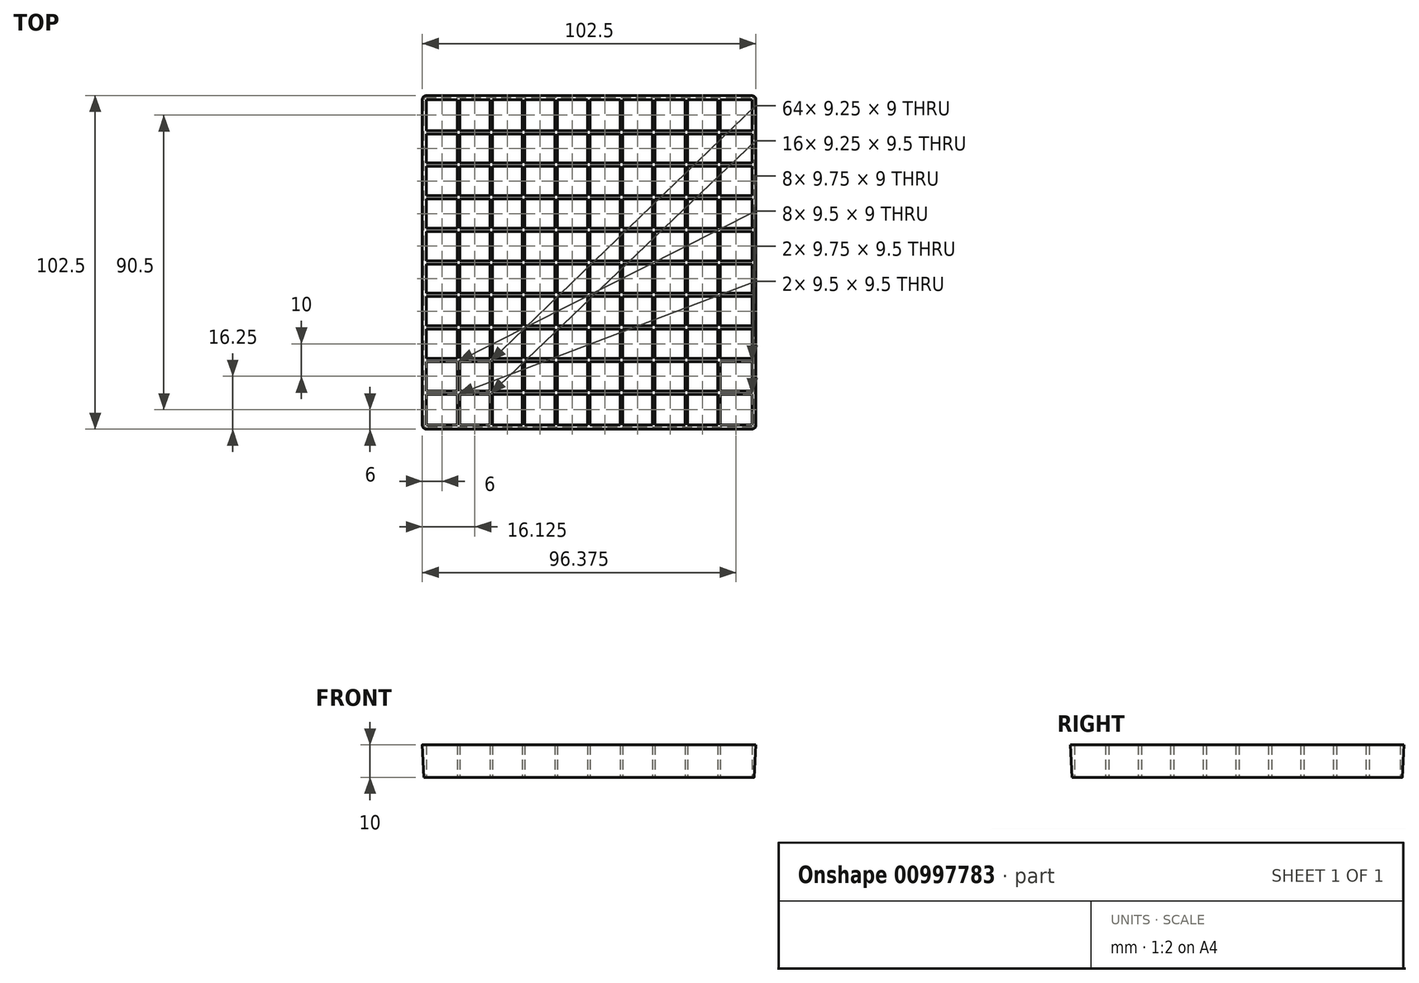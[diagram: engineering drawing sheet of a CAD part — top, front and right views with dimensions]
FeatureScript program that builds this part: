
annotation { "Feature Type Name" : "Feature", "Feature Type Description" : "" }
export const myFeature = defineFeature(function(context is Context, id is Id, definition is map)
    precondition{}
    {
        {
            assignVariable(context, id + "F0", {"name" : "p", "anyValue" : 1.5});
        }
        {
            var Q0;
            Q0=qCreatedBy(makeId("Top.planeOp"),FACE);
            var sketch = newSketch(context, id + "F1", { "sketchPlane" : qUnion([Q0])});
            skLineSegment(sketch, "E0.bottom", {"start": v(50, 50) * mm, "end": v(-50, 50) * mm});
            skLineSegment(sketch, "E0.top", {"start": v(50, -50) * mm, "end": v(-50, -50) * mm});
            skLineSegment(sketch, "E0.left", {"start": v(50, 50) * mm, "end": v(50, -50) * mm});
            skLineSegment(sketch, "E0.right", {"start": v(-50, 50) * mm, "end": v(-50, -50) * mm});
            skPoint(sketch, "E0.middle", {"position": v(0, 0) * mm});
            skLineSegment(sketch, "E1.bottom", {"start": v(-51.5, 51.5) * mm, "end": v(51.5, 51.5) * mm});
            skLineSegment(sketch, "E1.top", {"start": v(-51.5, -51.5) * mm, "end": v(51.5, -51.5) * mm});
            skLineSegment(sketch, "E1.left", {"start": v(-51.5, 51.5) * mm, "end": v(-51.5, -51.5) * mm});
            skLineSegment(sketch, "E1.right", {"start": v(51.5, 51.5) * mm, "end": v(51.5, -51.5) * mm});
            skLineSegment(sketch, "E2.bottom", {"start": v(-40.5, 50) * mm, "end": v(-39.75, 50) * mm});
            skLineSegment(sketch, "E2.top", {"start": v(-40.5, -50) * mm, "end": v(-39.75, -50) * mm});
            skLineSegment(sketch, "E2.left", {"start": v(-40.5, 50) * mm, "end": v(-40.5, -50) * mm});
            skLineSegment(sketch, "E2.right", {"start": v(-39.75, 50) * mm, "end": v(-39.75, -50) * mm});
            skLineSegment(sketch, "E3.1.0.0", {"start": v(-30.5, 50) * mm, "end": v(-30.5, -50) * mm});
            skLineSegment(sketch, "E3.1.0.1", {"start": v(-29.75, 50) * mm, "end": v(-29.75, -50) * mm});
            skLineSegment(sketch, "E3.2.0.0", {"start": v(-20.5, 50) * mm, "end": v(-20.5, -50) * mm});
            skLineSegment(sketch, "E3.2.0.1", {"start": v(-19.75, 50) * mm, "end": v(-19.75, -50) * mm});
            skLineSegment(sketch, "E3.3.0.0", {"start": v(-10.5, 50) * mm, "end": v(-10.5, -50) * mm});
            skLineSegment(sketch, "E3.3.0.1", {"start": v(-9.75, 50) * mm, "end": v(-9.75, -50) * mm});
            skLineSegment(sketch, "E3.4.0.0", {"start": v(-0.5, 50) * mm, "end": v(-0.5, -50) * mm});
            skLineSegment(sketch, "E3.4.0.1", {"start": v(0.25, 50) * mm, "end": v(0.25, -50) * mm});
            skLineSegment(sketch, "E3.5.0.0", {"start": v(9.5, 50) * mm, "end": v(9.5, -50) * mm});
            skLineSegment(sketch, "E3.5.0.1", {"start": v(10.25, 50) * mm, "end": v(10.25, -50) * mm});
            skLineSegment(sketch, "E3.6.0.0", {"start": v(19.5, 50) * mm, "end": v(19.5, -50) * mm});
            skLineSegment(sketch, "E3.6.0.1", {"start": v(20.25, 50) * mm, "end": v(20.25, -50) * mm});
            skLineSegment(sketch, "E3.7.0.0", {"start": v(29.5, 50) * mm, "end": v(29.5, -50) * mm});
            skLineSegment(sketch, "E3.7.0.1", {"start": v(30.25, 50) * mm, "end": v(30.25, -50) * mm});
            skLineSegment(sketch, "E3.8.0.0", {"start": v(39.5, 50) * mm, "end": v(39.5, -50) * mm});
            skLineSegment(sketch, "E3.8.0.1", {"start": v(40.25, 50) * mm, "end": v(40.25, -50) * mm});
            skLineSegment(sketch, "E3.direction1", {"start": v(-40.5, -50) * mm, "end": v(-30.5, -50) * mm, "construction": true});
            skLineSegment(sketch, "E4.bottom", {"start": v(-50, 40.5) * mm, "end": v(50, 40.5) * mm});
            skLineSegment(sketch, "E4.top", {"start": v(-50, 39.5) * mm, "end": v(50, 39.5) * mm});
            skLineSegment(sketch, "E4.left", {"start": v(-50, 40.5) * mm, "end": v(-50, 39.5) * mm});
            skLineSegment(sketch, "E4.right", {"start": v(50, 40.5) * mm, "end": v(50, 39.5) * mm});
            skLineSegment(sketch, "E5.0.1.0", {"start": v(-50, 30.5) * mm, "end": v(50, 30.5) * mm});
            skLineSegment(sketch, "E5.0.1.1", {"start": v(-50, 29.5) * mm, "end": v(50, 29.5) * mm});
            skLineSegment(sketch, "E5.0.2.0", {"start": v(-50, 20.5) * mm, "end": v(50, 20.5) * mm});
            skLineSegment(sketch, "E5.0.2.1", {"start": v(-50, 19.5) * mm, "end": v(50, 19.5) * mm});
            skLineSegment(sketch, "E5.0.3.0", {"start": v(-50, 10.5) * mm, "end": v(50, 10.5) * mm});
            skLineSegment(sketch, "E5.0.3.1", {"start": v(-50, 9.5) * mm, "end": v(50, 9.5) * mm});
            skLineSegment(sketch, "E5.0.4.0", {"start": v(-50, 0.5) * mm, "end": v(50, 0.5) * mm});
            skLineSegment(sketch, "E5.0.4.1", {"start": v(-50, -0.5) * mm, "end": v(50, -0.5) * mm});
            skLineSegment(sketch, "E5.0.5.0", {"start": v(-50, -9.5) * mm, "end": v(50, -9.5) * mm});
            skLineSegment(sketch, "E5.0.5.1", {"start": v(-50, -10.5) * mm, "end": v(50, -10.5) * mm});
            skLineSegment(sketch, "E5.0.6.0", {"start": v(-50, -19.5) * mm, "end": v(50, -19.5) * mm});
            skLineSegment(sketch, "E5.0.6.1", {"start": v(-50, -20.5) * mm, "end": v(50, -20.5) * mm});
            skLineSegment(sketch, "E5.0.7.0", {"start": v(-50, -29.5) * mm, "end": v(50, -29.5) * mm});
            skLineSegment(sketch, "E5.0.7.1", {"start": v(-50, -30.5) * mm, "end": v(50, -30.5) * mm});
            skLineSegment(sketch, "E5.0.8.0", {"start": v(-50, -39.5) * mm, "end": v(50, -39.5) * mm});
            skLineSegment(sketch, "E5.0.8.1", {"start": v(-50, -40.5) * mm, "end": v(50, -40.5) * mm});
            skLineSegment(sketch, "E5.direction1", {"start": v(-50, 40.5) * mm, "end": v(-25, 40.5) * mm, "construction": true});
            skLineSegment(sketch, "E5.direction2", {"start": v(-50, 40.5) * mm, "end": v(-50, 30.5) * mm, "construction": true});
            skSolve(sketch);
        }
        {
            var Q0;
            Q0=makeQuery(id+"F1.imprint","IMPRINT",FACE,{"disambiguationData":[TD([[makeQuery(id+"F1.imprint","IMPRINT",EDGE,{"derivedFrom":sQuery(id+"F1.wireOp",EDGE,"E1.bottom")}),-1.0]])]});
            extrude(context, id + "F2", {"entities" : qUnion([Q0]), "depth" : 10 * mm, "offsetDistance" : 25 * mm});
        }
        {
            var Q0;
            {var subQ0=sQuery(id+"F1.wireOp",EDGE,"E5.0.5.1");var subQ1=sQuery(id+"F1.wireOp",EDGE,"E3.1.0.0");var subQ2=makeQuery(id+"F1.imprint","INTERSECT",VERTEX,{"derivedFrom":[subQ1,subQ0]});Q0=makeQuery(id+"F1.imprint","IMPRINT",FACE,{"disambiguationData":[TD([[makeQuery(id+"F1.imprint","IMPRINT",EDGE,{"disambiguationData":[TD([[subQ2,-1.0]])],"derivedFrom":subQ1}),1.0]])]});}
            var Q1;
            {var subQ0=sQuery(id+"F1.wireOp",EDGE,"E5.0.6.1");var subQ1=sQuery(id+"F1.wireOp",EDGE,"E3.1.0.0");var subQ2=makeQuery(id+"F1.imprint","INTERSECT",VERTEX,{"derivedFrom":[subQ1,subQ0]});Q1=makeQuery(id+"F1.imprint","IMPRINT",FACE,{"disambiguationData":[TD([[makeQuery(id+"F1.imprint","IMPRINT",EDGE,{"disambiguationData":[TD([[subQ2,1.0]])],"derivedFrom":subQ1}),1.0]])]});}
            var Q2;
            {var subQ0=sQuery(id+"F1.wireOp",EDGE,"E5.0.2.1");var subQ1=sQuery(id+"F1.wireOp",EDGE,"E3.7.0.0");var subQ2=makeQuery(id+"F1.imprint","INTERSECT",VERTEX,{"derivedFrom":[subQ1,subQ0]});Q2=makeQuery(id+"F1.imprint","IMPRINT",FACE,{"disambiguationData":[TD([[makeQuery(id+"F1.imprint","IMPRINT",EDGE,{"disambiguationData":[TD([[subQ2,1.0]])],"derivedFrom":subQ1}),1.0]])]});}
            var Q3;
            {var subQ0=sQuery(id+"F1.wireOp",EDGE,"E5.0.4.0");var subQ1=sQuery(id+"F1.wireOp",EDGE,"E2.right");var subQ2=makeQuery(id+"F1.imprint","INTERSECT",VERTEX,{"derivedFrom":[subQ1,subQ0]});Q3=makeQuery(id+"F1.imprint","IMPRINT",FACE,{"disambiguationData":[TD([[makeQuery(id+"F1.imprint","IMPRINT",EDGE,{"disambiguationData":[TD([[subQ2,-1.0]])],"derivedFrom":subQ1}),1.0]])]});}
            var Q4;
            {var subQ0=sQuery(id+"F1.wireOp",EDGE,"E5.0.7.0");var subQ1=sQuery(id+"F1.wireOp",EDGE,"E3.1.0.1");var subQ2=makeQuery(id+"F1.imprint","INTERSECT",VERTEX,{"derivedFrom":[subQ1,subQ0]});Q4=makeQuery(id+"F1.imprint","IMPRINT",FACE,{"disambiguationData":[TD([[makeQuery(id+"F1.imprint","IMPRINT",EDGE,{"disambiguationData":[TD([[subQ2,-1.0]])],"derivedFrom":subQ1}),1.0]])]});}
            var Q5;
            {var subQ0=sQuery(id+"F1.wireOp",EDGE,"E5.0.5.0");var subQ1=sQuery(id+"F1.wireOp",EDGE,"E3.4.0.0");var subQ2=makeQuery(id+"F1.imprint","INTERSECT",VERTEX,{"derivedFrom":[subQ1,subQ0]});Q5=makeQuery(id+"F1.imprint","IMPRINT",FACE,{"disambiguationData":[TD([[makeQuery(id+"F1.imprint","IMPRINT",EDGE,{"disambiguationData":[TD([[subQ2,1.0]])],"derivedFrom":subQ1}),1.0]])]});}
            var Q6;
            {var subQ0=sQuery(id+"F1.wireOp",EDGE,"E5.0.7.0");var subQ1=sQuery(id+"F1.wireOp",EDGE,"E3.1.0.0");var subQ2=makeQuery(id+"F1.imprint","INTERSECT",VERTEX,{"derivedFrom":[subQ1,subQ0]});Q6=makeQuery(id+"F1.imprint","IMPRINT",FACE,{"disambiguationData":[TD([[makeQuery(id+"F1.imprint","IMPRINT",EDGE,{"disambiguationData":[TD([[subQ2,1.0]])],"derivedFrom":subQ1}),1.0]])]});}
            var Q7;
            {var subQ0=sQuery(id+"F1.wireOp",EDGE,"E5.0.5.0");var subQ1=sQuery(id+"F1.wireOp",EDGE,"E3.1.0.1");var subQ2=makeQuery(id+"F1.imprint","INTERSECT",VERTEX,{"derivedFrom":[subQ1,subQ0]});Q7=makeQuery(id+"F1.imprint","IMPRINT",FACE,{"disambiguationData":[TD([[makeQuery(id+"F1.imprint","IMPRINT",EDGE,{"disambiguationData":[TD([[subQ2,-1.0]])],"derivedFrom":subQ1}),1.0]])]});}
            var Q8;
            {var subQ0=sQuery(id+"F1.wireOp",EDGE,"E5.0.1.1");var subQ1=sQuery(id+"F1.wireOp",EDGE,"E2.left");var subQ2=makeQuery(id+"F1.imprint","INTERSECT",VERTEX,{"derivedFrom":[subQ1,subQ0]});Q8=makeQuery(id+"F1.imprint","IMPRINT",FACE,{"disambiguationData":[TD([[makeQuery(id+"F1.imprint","IMPRINT",EDGE,{"disambiguationData":[TD([[subQ2,1.0]])],"derivedFrom":subQ1}),1.0]])]});}
            var Q9;
            {var subQ0=sQuery(id+"F1.wireOp",EDGE,"E5.0.2.1");var subQ1=sQuery(id+"F1.wireOp",EDGE,"E3.4.0.1");var subQ2=makeQuery(id+"F1.imprint","INTERSECT",VERTEX,{"derivedFrom":[subQ1,subQ0]});Q9=makeQuery(id+"F1.imprint","IMPRINT",FACE,{"disambiguationData":[TD([[makeQuery(id+"F1.imprint","IMPRINT",EDGE,{"disambiguationData":[TD([[subQ2,1.0]])],"derivedFrom":subQ1}),1.0]])]});}
            var Q10;
            {var subQ0=sQuery(id+"F1.wireOp",EDGE,"E5.0.1.0");var subQ1=sQuery(id+"F1.wireOp",EDGE,"E3.1.0.1");var subQ2=makeQuery(id+"F1.imprint","INTERSECT",VERTEX,{"derivedFrom":[subQ1,subQ0]});Q10=makeQuery(id+"F1.imprint","IMPRINT",FACE,{"disambiguationData":[TD([[makeQuery(id+"F1.imprint","IMPRINT",EDGE,{"disambiguationData":[TD([[subQ2,-1.0]])],"derivedFrom":subQ1}),1.0]])]});}
            var Q11;
            {var subQ0=sQuery(id+"F1.wireOp",EDGE,"E5.0.8.0");var subQ1=sQuery(id+"F1.wireOp",EDGE,"E3.6.0.0");var subQ2=makeQuery(id+"F1.imprint","INTERSECT",VERTEX,{"derivedFrom":[subQ1,subQ0]});Q11=makeQuery(id+"F1.imprint","IMPRINT",FACE,{"disambiguationData":[TD([[makeQuery(id+"F1.imprint","IMPRINT",EDGE,{"disambiguationData":[TD([[subQ2,1.0]])],"derivedFrom":subQ1}),1.0]])]});}
            var Q12;
            {var subQ0=sQuery(id+"F1.wireOp",EDGE,"E5.0.1.1");var subQ1=sQuery(id+"F1.wireOp",EDGE,"E2.right");var subQ2=makeQuery(id+"F1.imprint","INTERSECT",VERTEX,{"derivedFrom":[subQ1,subQ0]});Q12=makeQuery(id+"F1.imprint","IMPRINT",FACE,{"disambiguationData":[TD([[makeQuery(id+"F1.imprint","IMPRINT",EDGE,{"disambiguationData":[TD([[subQ2,1.0]])],"derivedFrom":subQ1}),1.0]])]});}
            var Q13;
            {var subQ0=sQuery(id+"F1.wireOp",EDGE,"E5.0.3.1");var subQ1=sQuery(id+"F1.wireOp",EDGE,"E3.8.0.0");var subQ2=makeQuery(id+"F1.imprint","INTERSECT",VERTEX,{"derivedFrom":[subQ1,subQ0]});Q13=makeQuery(id+"F1.imprint","IMPRINT",FACE,{"disambiguationData":[TD([[makeQuery(id+"F1.imprint","IMPRINT",EDGE,{"disambiguationData":[TD([[subQ2,1.0]])],"derivedFrom":subQ1}),1.0]])]});}
            var Q14;
            {var subQ0=sQuery(id+"F1.wireOp",EDGE,"E5.0.2.0");var subQ1=sQuery(id+"F1.wireOp",EDGE,"E3.1.0.0");var subQ2=makeQuery(id+"F1.imprint","INTERSECT",VERTEX,{"derivedFrom":[subQ1,subQ0]});Q14=makeQuery(id+"F1.imprint","IMPRINT",FACE,{"disambiguationData":[TD([[makeQuery(id+"F1.imprint","IMPRINT",EDGE,{"disambiguationData":[TD([[subQ2,-1.0]])],"derivedFrom":subQ1}),1.0]])]});}
            var Q15;
            {var subQ0=sQuery(id+"F1.wireOp",EDGE,"E5.0.6.1");var subQ1=sQuery(id+"F1.wireOp",EDGE,"E3.2.0.0");var subQ2=makeQuery(id+"F1.imprint","INTERSECT",VERTEX,{"derivedFrom":[subQ1,subQ0]});Q15=makeQuery(id+"F1.imprint","IMPRINT",FACE,{"disambiguationData":[TD([[makeQuery(id+"F1.imprint","IMPRINT",EDGE,{"disambiguationData":[TD([[subQ2,1.0]])],"derivedFrom":subQ1}),1.0]])]});}
            var Q16;
            {var subQ0=sQuery(id+"F1.wireOp",EDGE,"E5.0.4.0");var subQ1=sQuery(id+"F1.wireOp",EDGE,"E3.1.0.1");var subQ2=makeQuery(id+"F1.imprint","INTERSECT",VERTEX,{"derivedFrom":[subQ1,subQ0]});Q16=makeQuery(id+"F1.imprint","IMPRINT",FACE,{"disambiguationData":[TD([[makeQuery(id+"F1.imprint","IMPRINT",EDGE,{"disambiguationData":[TD([[subQ2,-1.0]])],"derivedFrom":subQ1}),1.0]])]});}
            var Q17;
            {var subQ0=sQuery(id+"F1.wireOp",EDGE,"E5.0.6.0");var subQ1=sQuery(id+"F1.wireOp",EDGE,"E3.8.0.0");var subQ2=makeQuery(id+"F1.imprint","INTERSECT",VERTEX,{"derivedFrom":[subQ1,subQ0]});Q17=makeQuery(id+"F1.imprint","IMPRINT",FACE,{"disambiguationData":[TD([[makeQuery(id+"F1.imprint","IMPRINT",EDGE,{"disambiguationData":[TD([[subQ2,1.0]])],"derivedFrom":subQ1}),1.0]])]});}
            var Q18;
            {var subQ0=sQuery(id+"F1.wireOp",EDGE,"E5.0.4.1");var subQ1=sQuery(id+"F1.wireOp",EDGE,"E3.6.0.1");var subQ2=makeQuery(id+"F1.imprint","INTERSECT",VERTEX,{"derivedFrom":[subQ1,subQ0]});Q18=makeQuery(id+"F1.imprint","IMPRINT",FACE,{"disambiguationData":[TD([[makeQuery(id+"F1.imprint","IMPRINT",EDGE,{"disambiguationData":[TD([[subQ2,1.0]])],"derivedFrom":subQ1}),1.0]])]});}
            var Q19;
            {var subQ0=sQuery(id+"F1.wireOp",EDGE,"E5.0.3.1");var subQ1=sQuery(id+"F1.wireOp",EDGE,"E3.4.0.0");var subQ2=makeQuery(id+"F1.imprint","INTERSECT",VERTEX,{"derivedFrom":[subQ1,subQ0]});Q19=makeQuery(id+"F1.imprint","IMPRINT",FACE,{"disambiguationData":[TD([[makeQuery(id+"F1.imprint","IMPRINT",EDGE,{"disambiguationData":[TD([[subQ2,1.0]])],"derivedFrom":subQ1}),1.0]])]});}
            var Q20;
            {var subQ0=sQuery(id+"F1.wireOp",EDGE,"E5.0.7.0");var subQ1=sQuery(id+"F1.wireOp",EDGE,"E3.3.0.1");var subQ2=makeQuery(id+"F1.imprint","INTERSECT",VERTEX,{"derivedFrom":[subQ1,subQ0]});Q20=makeQuery(id+"F1.imprint","IMPRINT",FACE,{"disambiguationData":[TD([[makeQuery(id+"F1.imprint","IMPRINT",EDGE,{"disambiguationData":[TD([[subQ2,-1.0]])],"derivedFrom":subQ1}),1.0]])]});}
            var Q21;
            {var subQ0=sQuery(id+"F1.wireOp",EDGE,"E5.0.1.1");var subQ1=sQuery(id+"F1.wireOp",EDGE,"E3.5.0.0");var subQ2=makeQuery(id+"F1.imprint","INTERSECT",VERTEX,{"derivedFrom":[subQ1,subQ0]});Q21=makeQuery(id+"F1.imprint","IMPRINT",FACE,{"disambiguationData":[TD([[makeQuery(id+"F1.imprint","IMPRINT",EDGE,{"disambiguationData":[TD([[subQ2,1.0]])],"derivedFrom":subQ1}),1.0]])]});}
            var Q22;
            {var subQ0=sQuery(id+"F1.wireOp",EDGE,"E5.0.1.1");var subQ1=sQuery(id+"F1.wireOp",EDGE,"E3.6.0.1");var subQ2=makeQuery(id+"F1.imprint","INTERSECT",VERTEX,{"derivedFrom":[subQ1,subQ0]});Q22=makeQuery(id+"F1.imprint","IMPRINT",FACE,{"disambiguationData":[TD([[makeQuery(id+"F1.imprint","IMPRINT",EDGE,{"disambiguationData":[TD([[subQ2,1.0]])],"derivedFrom":subQ1}),1.0]])]});}
            var Q23;
            {var subQ0=sQuery(id+"F1.wireOp",EDGE,"E4.bottom");var subQ1=sQuery(id+"F1.wireOp",EDGE,"E3.8.0.0");var subQ2=makeQuery(id+"F1.imprint","INTERSECT",VERTEX,{"derivedFrom":[subQ1,subQ0]});Q23=makeQuery(id+"F1.imprint","IMPRINT",FACE,{"disambiguationData":[TD([[makeQuery(id+"F1.imprint","IMPRINT",EDGE,{"disambiguationData":[TD([[subQ2,-1.0]])],"derivedFrom":subQ1}),1.0]])]});}
            var Q24;
            {var subQ0=sQuery(id+"F1.wireOp",EDGE,"E5.0.2.0");var subQ1=sQuery(id+"F1.wireOp",EDGE,"E3.7.0.1");var subQ2=makeQuery(id+"F1.imprint","INTERSECT",VERTEX,{"derivedFrom":[subQ1,subQ0]});Q24=makeQuery(id+"F1.imprint","IMPRINT",FACE,{"disambiguationData":[TD([[makeQuery(id+"F1.imprint","IMPRINT",EDGE,{"disambiguationData":[TD([[subQ2,-1.0]])],"derivedFrom":subQ1}),1.0]])]});}
            var Q25;
            {var subQ0=sQuery(id+"F1.wireOp",EDGE,"E5.0.5.1");var subQ1=sQuery(id+"F1.wireOp",EDGE,"E3.5.0.0");var subQ2=makeQuery(id+"F1.imprint","INTERSECT",VERTEX,{"derivedFrom":[subQ1,subQ0]});Q25=makeQuery(id+"F1.imprint","IMPRINT",FACE,{"disambiguationData":[TD([[makeQuery(id+"F1.imprint","IMPRINT",EDGE,{"disambiguationData":[TD([[subQ2,-1.0]])],"derivedFrom":subQ1}),1.0]])]});}
            var Q26;
            {var subQ0=sQuery(id+"F1.wireOp",EDGE,"E5.0.5.1");var subQ1=sQuery(id+"F1.wireOp",EDGE,"E3.6.0.0");var subQ2=makeQuery(id+"F1.imprint","INTERSECT",VERTEX,{"derivedFrom":[subQ1,subQ0]});Q26=makeQuery(id+"F1.imprint","IMPRINT",FACE,{"disambiguationData":[TD([[makeQuery(id+"F1.imprint","IMPRINT",EDGE,{"disambiguationData":[TD([[subQ2,-1.0]])],"derivedFrom":subQ1}),1.0]])]});}
            var Q27;
            {var subQ0=sQuery(id+"F1.wireOp",EDGE,"E5.0.2.0");var subQ1=sQuery(id+"F1.wireOp",EDGE,"E2.left");var subQ2=makeQuery(id+"F1.imprint","INTERSECT",VERTEX,{"derivedFrom":[subQ1,subQ0]});Q27=makeQuery(id+"F1.imprint","IMPRINT",FACE,{"disambiguationData":[TD([[makeQuery(id+"F1.imprint","IMPRINT",EDGE,{"disambiguationData":[TD([[subQ2,1.0]])],"derivedFrom":subQ1}),1.0]])]});}
            var Q28;
            {var subQ0=sQuery(id+"F1.wireOp",EDGE,"E5.0.4.1");var subQ1=sQuery(id+"F1.wireOp",EDGE,"E3.6.0.0");var subQ2=makeQuery(id+"F1.imprint","INTERSECT",VERTEX,{"derivedFrom":[subQ1,subQ0]});Q28=makeQuery(id+"F1.imprint","IMPRINT",FACE,{"disambiguationData":[TD([[makeQuery(id+"F1.imprint","IMPRINT",EDGE,{"disambiguationData":[TD([[subQ2,1.0]])],"derivedFrom":subQ1}),1.0]])]});}
            var Q29;
            {var subQ0=sQuery(id+"F1.wireOp",EDGE,"E5.0.6.1");var subQ1=sQuery(id+"F1.wireOp",EDGE,"E3.5.0.0");var subQ2=makeQuery(id+"F1.imprint","INTERSECT",VERTEX,{"derivedFrom":[subQ1,subQ0]});Q29=makeQuery(id+"F1.imprint","IMPRINT",FACE,{"disambiguationData":[TD([[makeQuery(id+"F1.imprint","IMPRINT",EDGE,{"disambiguationData":[TD([[subQ2,1.0]])],"derivedFrom":subQ1}),1.0]])]});}
            var Q30;
            {var subQ0=sQuery(id+"F1.wireOp",EDGE,"E4.top");var subQ1=sQuery(id+"F1.wireOp",EDGE,"E3.4.0.1");var subQ2=makeQuery(id+"F1.imprint","INTERSECT",VERTEX,{"derivedFrom":[subQ1,subQ0]});Q30=makeQuery(id+"F1.imprint","IMPRINT",FACE,{"disambiguationData":[TD([[makeQuery(id+"F1.imprint","IMPRINT",EDGE,{"disambiguationData":[TD([[subQ2,1.0]])],"derivedFrom":subQ1}),1.0]])]});}
            var Q31;
            {var subQ0=sQuery(id+"F1.wireOp",EDGE,"E5.0.1.1");var subQ1=sQuery(id+"F1.wireOp",EDGE,"E3.2.0.0");var subQ2=makeQuery(id+"F1.imprint","INTERSECT",VERTEX,{"derivedFrom":[subQ1,subQ0]});Q31=makeQuery(id+"F1.imprint","IMPRINT",FACE,{"disambiguationData":[TD([[makeQuery(id+"F1.imprint","IMPRINT",EDGE,{"disambiguationData":[TD([[subQ2,-1.0]])],"derivedFrom":subQ1}),1.0]])]});}
            var Q32;
            {var subQ0=sQuery(id+"F1.wireOp",EDGE,"E5.0.1.1");var subQ1=sQuery(id+"F1.wireOp",EDGE,"E3.4.0.0");var subQ2=makeQuery(id+"F1.imprint","INTERSECT",VERTEX,{"derivedFrom":[subQ1,subQ0]});Q32=makeQuery(id+"F1.imprint","IMPRINT",FACE,{"disambiguationData":[TD([[makeQuery(id+"F1.imprint","IMPRINT",EDGE,{"disambiguationData":[TD([[subQ2,1.0]])],"derivedFrom":subQ1}),1.0]])]});}
            var Q33;
            {var subQ0=sQuery(id+"F1.wireOp",EDGE,"E4.top");var subQ1=sQuery(id+"F1.wireOp",EDGE,"E3.4.0.0");var subQ2=makeQuery(id+"F1.imprint","INTERSECT",VERTEX,{"derivedFrom":[subQ1,subQ0]});Q33=makeQuery(id+"F1.imprint","IMPRINT",FACE,{"disambiguationData":[TD([[makeQuery(id+"F1.imprint","IMPRINT",EDGE,{"disambiguationData":[TD([[subQ2,-1.0]])],"derivedFrom":subQ1}),1.0]])]});}
            var Q34;
            {var subQ0=sQuery(id+"F1.wireOp",EDGE,"E5.0.7.0");var subQ1=sQuery(id+"F1.wireOp",EDGE,"E3.5.0.0");var subQ2=makeQuery(id+"F1.imprint","INTERSECT",VERTEX,{"derivedFrom":[subQ1,subQ0]});Q34=makeQuery(id+"F1.imprint","IMPRINT",FACE,{"disambiguationData":[TD([[makeQuery(id+"F1.imprint","IMPRINT",EDGE,{"disambiguationData":[TD([[subQ2,-1.0]])],"derivedFrom":subQ1}),1.0]])]});}
            var Q35;
            {var subQ0=sQuery(id+"F1.wireOp",EDGE,"E5.0.1.1");var subQ1=sQuery(id+"F1.wireOp",EDGE,"E3.5.0.1");var subQ2=makeQuery(id+"F1.imprint","INTERSECT",VERTEX,{"derivedFrom":[subQ1,subQ0]});Q35=makeQuery(id+"F1.imprint","IMPRINT",FACE,{"disambiguationData":[TD([[makeQuery(id+"F1.imprint","IMPRINT",EDGE,{"disambiguationData":[TD([[subQ2,1.0]])],"derivedFrom":subQ1}),1.0]])]});}
            var Q36;
            {var subQ0=sQuery(id+"F1.wireOp",EDGE,"E5.0.5.0");var subQ1=sQuery(id+"F1.wireOp",EDGE,"E3.5.0.0");var subQ2=makeQuery(id+"F1.imprint","INTERSECT",VERTEX,{"derivedFrom":[subQ1,subQ0]});Q36=makeQuery(id+"F1.imprint","IMPRINT",FACE,{"disambiguationData":[TD([[makeQuery(id+"F1.imprint","IMPRINT",EDGE,{"disambiguationData":[TD([[subQ2,1.0]])],"derivedFrom":subQ1}),1.0]])]});}
            var Q37;
            {var subQ0=sQuery(id+"F1.wireOp",EDGE,"E5.0.8.1");var subQ1=sQuery(id+"F1.wireOp",EDGE,"E3.2.0.1");var subQ2=makeQuery(id+"F1.imprint","INTERSECT",VERTEX,{"derivedFrom":[subQ1,subQ0]});Q37=makeQuery(id+"F1.imprint","IMPRINT",FACE,{"disambiguationData":[TD([[makeQuery(id+"F1.imprint","IMPRINT",EDGE,{"disambiguationData":[TD([[subQ2,1.0]])],"derivedFrom":subQ1}),1.0]])]});}
            var Q38;
            {var subQ0=sQuery(id+"F1.wireOp",EDGE,"E5.0.6.1");var subQ1=sQuery(id+"F1.wireOp",EDGE,"E3.6.0.1");var subQ2=makeQuery(id+"F1.imprint","INTERSECT",VERTEX,{"derivedFrom":[subQ1,subQ0]});Q38=makeQuery(id+"F1.imprint","IMPRINT",FACE,{"disambiguationData":[TD([[makeQuery(id+"F1.imprint","IMPRINT",EDGE,{"disambiguationData":[TD([[subQ2,1.0]])],"derivedFrom":subQ1}),1.0]])]});}
            var Q39;
            {var subQ0=sQuery(id+"F1.wireOp",EDGE,"E4.bottom");var subQ1=sQuery(id+"F1.wireOp",EDGE,"E2.right");var subQ2=makeQuery(id+"F1.imprint","INTERSECT",VERTEX,{"derivedFrom":[subQ1,subQ0]});Q39=makeQuery(id+"F1.imprint","IMPRINT",FACE,{"disambiguationData":[TD([[makeQuery(id+"F1.imprint","IMPRINT",EDGE,{"disambiguationData":[TD([[subQ2,-1.0]])],"derivedFrom":subQ1}),1.0]])]});}
            var Q40;
            {var subQ0=sQuery(id+"F1.wireOp",EDGE,"E5.0.2.1");var subQ1=sQuery(id+"F1.wireOp",EDGE,"E2.left");var subQ2=makeQuery(id+"F1.imprint","INTERSECT",VERTEX,{"derivedFrom":[subQ1,subQ0]});Q40=makeQuery(id+"F1.imprint","IMPRINT",FACE,{"disambiguationData":[TD([[makeQuery(id+"F1.imprint","IMPRINT",EDGE,{"disambiguationData":[TD([[subQ2,-1.0]])],"derivedFrom":subQ1}),1.0]])]});}
            var Q41;
            {var subQ0=sQuery(id+"F1.wireOp",EDGE,"E4.bottom");var subQ1=sQuery(id+"F1.wireOp",EDGE,"E3.6.0.0");var subQ2=makeQuery(id+"F1.imprint","INTERSECT",VERTEX,{"derivedFrom":[subQ1,subQ0]});Q41=makeQuery(id+"F1.imprint","IMPRINT",FACE,{"disambiguationData":[TD([[makeQuery(id+"F1.imprint","IMPRINT",EDGE,{"disambiguationData":[TD([[subQ2,-1.0]])],"derivedFrom":subQ1}),1.0]])]});}
            var Q42;
            {var subQ0=sQuery(id+"F1.wireOp",EDGE,"E4.bottom");var subQ1=sQuery(id+"F1.wireOp",EDGE,"E3.6.0.1");var subQ2=makeQuery(id+"F1.imprint","INTERSECT",VERTEX,{"derivedFrom":[subQ1,subQ0]});Q42=makeQuery(id+"F1.imprint","IMPRINT",FACE,{"disambiguationData":[TD([[makeQuery(id+"F1.imprint","IMPRINT",EDGE,{"disambiguationData":[TD([[subQ2,-1.0]])],"derivedFrom":subQ1}),1.0]])]});}
            var Q43;
            {var subQ0=sQuery(id+"F1.wireOp",EDGE,"E5.0.7.0");var subQ1=sQuery(id+"F1.wireOp",EDGE,"E3.6.0.0");var subQ2=makeQuery(id+"F1.imprint","INTERSECT",VERTEX,{"derivedFrom":[subQ1,subQ0]});Q43=makeQuery(id+"F1.imprint","IMPRINT",FACE,{"disambiguationData":[TD([[makeQuery(id+"F1.imprint","IMPRINT",EDGE,{"disambiguationData":[TD([[subQ2,1.0]])],"derivedFrom":subQ1}),1.0]])]});}
            var Q44;
            {var subQ0=sQuery(id+"F1.wireOp",EDGE,"E5.0.5.0");var subQ1=sQuery(id+"F1.wireOp",EDGE,"E3.3.0.1");var subQ2=makeQuery(id+"F1.imprint","INTERSECT",VERTEX,{"derivedFrom":[subQ1,subQ0]});Q44=makeQuery(id+"F1.imprint","IMPRINT",FACE,{"disambiguationData":[TD([[makeQuery(id+"F1.imprint","IMPRINT",EDGE,{"disambiguationData":[TD([[subQ2,-1.0]])],"derivedFrom":subQ1}),1.0]])]});}
            var Q45;
            {var subQ0=sQuery(id+"F1.wireOp",EDGE,"E5.0.8.1");var subQ1=sQuery(id+"F1.wireOp",EDGE,"E3.1.0.1");var subQ2=makeQuery(id+"F1.imprint","INTERSECT",VERTEX,{"derivedFrom":[subQ1,subQ0]});Q45=makeQuery(id+"F1.imprint","IMPRINT",FACE,{"disambiguationData":[TD([[makeQuery(id+"F1.imprint","IMPRINT",EDGE,{"disambiguationData":[TD([[subQ2,1.0]])],"derivedFrom":subQ1}),1.0]])]});}
            var Q46;
            {var subQ0=sQuery(id+"F1.wireOp",EDGE,"E5.0.5.0");var subQ1=sQuery(id+"F1.wireOp",EDGE,"E3.1.0.0");var subQ2=makeQuery(id+"F1.imprint","INTERSECT",VERTEX,{"derivedFrom":[subQ1,subQ0]});Q46=makeQuery(id+"F1.imprint","IMPRINT",FACE,{"disambiguationData":[TD([[makeQuery(id+"F1.imprint","IMPRINT",EDGE,{"disambiguationData":[TD([[subQ2,-1.0]])],"derivedFrom":subQ1}),1.0]])]});}
            var Q47;
            {var subQ0=sQuery(id+"F1.wireOp",EDGE,"E5.0.2.0");var subQ1=sQuery(id+"F1.wireOp",EDGE,"E3.4.0.0");var subQ2=makeQuery(id+"F1.imprint","INTERSECT",VERTEX,{"derivedFrom":[subQ1,subQ0]});Q47=makeQuery(id+"F1.imprint","IMPRINT",FACE,{"disambiguationData":[TD([[makeQuery(id+"F1.imprint","IMPRINT",EDGE,{"disambiguationData":[TD([[subQ2,1.0]])],"derivedFrom":subQ1}),1.0]])]});}
            var Q48;
            {var subQ0=sQuery(id+"F1.wireOp",EDGE,"E5.0.7.1");var subQ1=sQuery(id+"F1.wireOp",EDGE,"E3.5.0.0");var subQ2=makeQuery(id+"F1.imprint","INTERSECT",VERTEX,{"derivedFrom":[subQ1,subQ0]});Q48=makeQuery(id+"F1.imprint","IMPRINT",FACE,{"disambiguationData":[TD([[makeQuery(id+"F1.imprint","IMPRINT",EDGE,{"disambiguationData":[TD([[subQ2,-1.0]])],"derivedFrom":subQ1}),1.0]])]});}
            var Q49;
            {var subQ0=sQuery(id+"F1.wireOp",EDGE,"E5.0.8.1");var subQ1=sQuery(id+"F1.wireOp",EDGE,"E3.8.0.0");var subQ2=makeQuery(id+"F1.imprint","INTERSECT",VERTEX,{"derivedFrom":[subQ1,subQ0]});Q49=makeQuery(id+"F1.imprint","IMPRINT",FACE,{"disambiguationData":[TD([[makeQuery(id+"F1.imprint","IMPRINT",EDGE,{"disambiguationData":[TD([[subQ2,1.0]])],"derivedFrom":subQ1}),1.0]])]});}
            var Q50;
            {var subQ0=sQuery(id+"F1.wireOp",EDGE,"E5.0.4.0");var subQ1=sQuery(id+"F1.wireOp",EDGE,"E3.5.0.0");var subQ2=makeQuery(id+"F1.imprint","INTERSECT",VERTEX,{"derivedFrom":[subQ1,subQ0]});Q50=makeQuery(id+"F1.imprint","IMPRINT",FACE,{"disambiguationData":[TD([[makeQuery(id+"F1.imprint","IMPRINT",EDGE,{"disambiguationData":[TD([[subQ2,-1.0]])],"derivedFrom":subQ1}),1.0]])]});}
            var Q51;
            {var subQ0=sQuery(id+"F1.wireOp",EDGE,"E5.0.6.1");var subQ1=sQuery(id+"F1.wireOp",EDGE,"E3.2.0.0");var subQ2=makeQuery(id+"F1.imprint","INTERSECT",VERTEX,{"derivedFrom":[subQ1,subQ0]});Q51=makeQuery(id+"F1.imprint","IMPRINT",FACE,{"disambiguationData":[TD([[makeQuery(id+"F1.imprint","IMPRINT",EDGE,{"disambiguationData":[TD([[subQ2,-1.0]])],"derivedFrom":subQ1}),1.0]])]});}
            var Q52;
            {var subQ0=sQuery(id+"F1.wireOp",EDGE,"E5.0.8.1");var subQ1=sQuery(id+"F1.wireOp",EDGE,"E2.right");var subQ2=makeQuery(id+"F1.imprint","INTERSECT",VERTEX,{"derivedFrom":[subQ1,subQ0]});Q52=makeQuery(id+"F1.imprint","IMPRINT",FACE,{"disambiguationData":[TD([[makeQuery(id+"F1.imprint","IMPRINT",EDGE,{"disambiguationData":[TD([[subQ2,1.0]])],"derivedFrom":subQ1}),1.0]])]});}
            var Q53;
            {var subQ0=sQuery(id+"F1.wireOp",EDGE,"E5.0.2.1");var subQ1=sQuery(id+"F1.wireOp",EDGE,"E3.5.0.0");var subQ2=makeQuery(id+"F1.imprint","INTERSECT",VERTEX,{"derivedFrom":[subQ1,subQ0]});Q53=makeQuery(id+"F1.imprint","IMPRINT",FACE,{"disambiguationData":[TD([[makeQuery(id+"F1.imprint","IMPRINT",EDGE,{"disambiguationData":[TD([[subQ2,-1.0]])],"derivedFrom":subQ1}),1.0]])]});}
            var Q54;
            {var subQ0=sQuery(id+"F1.wireOp",EDGE,"E5.0.4.1");var subQ1=sQuery(id+"F1.wireOp",EDGE,"E3.8.0.0");var subQ2=makeQuery(id+"F1.imprint","INTERSECT",VERTEX,{"derivedFrom":[subQ1,subQ0]});Q54=makeQuery(id+"F1.imprint","IMPRINT",FACE,{"disambiguationData":[TD([[makeQuery(id+"F1.imprint","IMPRINT",EDGE,{"disambiguationData":[TD([[subQ2,-1.0]])],"derivedFrom":subQ1}),1.0]])]});}
            var Q55;
            {var subQ0=sQuery(id+"F1.wireOp",EDGE,"E5.0.8.1");var subQ1=sQuery(id+"F1.wireOp",EDGE,"E3.6.0.1");var subQ2=makeQuery(id+"F1.imprint","INTERSECT",VERTEX,{"derivedFrom":[subQ1,subQ0]});Q55=makeQuery(id+"F1.imprint","IMPRINT",FACE,{"disambiguationData":[TD([[makeQuery(id+"F1.imprint","IMPRINT",EDGE,{"disambiguationData":[TD([[subQ2,1.0]])],"derivedFrom":subQ1}),1.0]])]});}
            var Q56;
            {var subQ0=sQuery(id+"F1.wireOp",EDGE,"E5.0.1.1");var subQ1=sQuery(id+"F1.wireOp",EDGE,"E3.3.0.1");var subQ2=makeQuery(id+"F1.imprint","INTERSECT",VERTEX,{"derivedFrom":[subQ1,subQ0]});Q56=makeQuery(id+"F1.imprint","IMPRINT",FACE,{"disambiguationData":[TD([[makeQuery(id+"F1.imprint","IMPRINT",EDGE,{"disambiguationData":[TD([[subQ2,1.0]])],"derivedFrom":subQ1}),1.0]])]});}
            var Q57;
            {var subQ0=sQuery(id+"F1.wireOp",EDGE,"E5.0.8.1");var subQ1=sQuery(id+"F1.wireOp",EDGE,"E3.3.0.0");var subQ2=makeQuery(id+"F1.imprint","INTERSECT",VERTEX,{"derivedFrom":[subQ1,subQ0]});Q57=makeQuery(id+"F1.imprint","IMPRINT",FACE,{"disambiguationData":[TD([[makeQuery(id+"F1.imprint","IMPRINT",EDGE,{"disambiguationData":[TD([[subQ2,1.0]])],"derivedFrom":subQ1}),1.0]])]});}
            var Q58;
            {var subQ0=sQuery(id+"F1.wireOp",EDGE,"E5.0.7.0");var subQ1=sQuery(id+"F1.wireOp",EDGE,"E3.1.0.0");var subQ2=makeQuery(id+"F1.imprint","INTERSECT",VERTEX,{"derivedFrom":[subQ1,subQ0]});Q58=makeQuery(id+"F1.imprint","IMPRINT",FACE,{"disambiguationData":[TD([[makeQuery(id+"F1.imprint","IMPRINT",EDGE,{"disambiguationData":[TD([[subQ2,-1.0]])],"derivedFrom":subQ1}),1.0]])]});}
            var Q59;
            {var subQ0=sQuery(id+"F1.wireOp",EDGE,"E5.0.6.0");var subQ1=sQuery(id+"F1.wireOp",EDGE,"E3.2.0.0");var subQ2=makeQuery(id+"F1.imprint","INTERSECT",VERTEX,{"derivedFrom":[subQ1,subQ0]});Q59=makeQuery(id+"F1.imprint","IMPRINT",FACE,{"disambiguationData":[TD([[makeQuery(id+"F1.imprint","IMPRINT",EDGE,{"disambiguationData":[TD([[subQ2,1.0]])],"derivedFrom":subQ1}),1.0]])]});}
            var Q60;
            {var subQ0=sQuery(id+"F1.wireOp",EDGE,"E5.0.8.1");var subQ1=sQuery(id+"F1.wireOp",EDGE,"E3.5.0.0");var subQ2=makeQuery(id+"F1.imprint","INTERSECT",VERTEX,{"derivedFrom":[subQ1,subQ0]});Q60=makeQuery(id+"F1.imprint","IMPRINT",FACE,{"disambiguationData":[TD([[makeQuery(id+"F1.imprint","IMPRINT",EDGE,{"disambiguationData":[TD([[subQ2,1.0]])],"derivedFrom":subQ1}),1.0]])]});}
            var Q61;
            {var subQ0=sQuery(id+"F1.wireOp",EDGE,"E5.0.3.1");var subQ1=sQuery(id+"F1.wireOp",EDGE,"E3.6.0.0");var subQ2=makeQuery(id+"F1.imprint","INTERSECT",VERTEX,{"derivedFrom":[subQ1,subQ0]});Q61=makeQuery(id+"F1.imprint","IMPRINT",FACE,{"disambiguationData":[TD([[makeQuery(id+"F1.imprint","IMPRINT",EDGE,{"disambiguationData":[TD([[subQ2,1.0]])],"derivedFrom":subQ1}),1.0]])]});}
            var Q62;
            {var subQ0=sQuery(id+"F1.wireOp",EDGE,"E5.0.6.1");var subQ1=sQuery(id+"F1.wireOp",EDGE,"E3.5.0.1");var subQ2=makeQuery(id+"F1.imprint","INTERSECT",VERTEX,{"derivedFrom":[subQ1,subQ0]});Q62=makeQuery(id+"F1.imprint","IMPRINT",FACE,{"disambiguationData":[TD([[makeQuery(id+"F1.imprint","IMPRINT",EDGE,{"disambiguationData":[TD([[subQ2,1.0]])],"derivedFrom":subQ1}),1.0]])]});}
            var Q63;
            {var subQ0=sQuery(id+"F1.wireOp",EDGE,"E5.0.4.0");var subQ1=sQuery(id+"F1.wireOp",EDGE,"E3.5.0.0");var subQ2=makeQuery(id+"F1.imprint","INTERSECT",VERTEX,{"derivedFrom":[subQ1,subQ0]});Q63=makeQuery(id+"F1.imprint","IMPRINT",FACE,{"disambiguationData":[TD([[makeQuery(id+"F1.imprint","IMPRINT",EDGE,{"disambiguationData":[TD([[subQ2,1.0]])],"derivedFrom":subQ1}),1.0]])]});}
            var Q64;
            {var subQ0=sQuery(id+"F1.wireOp",EDGE,"E5.0.7.0");var subQ1=sQuery(id+"F1.wireOp",EDGE,"E3.7.0.1");var subQ2=makeQuery(id+"F1.imprint","INTERSECT",VERTEX,{"derivedFrom":[subQ1,subQ0]});Q64=makeQuery(id+"F1.imprint","IMPRINT",FACE,{"disambiguationData":[TD([[makeQuery(id+"F1.imprint","IMPRINT",EDGE,{"disambiguationData":[TD([[subQ2,-1.0]])],"derivedFrom":subQ1}),1.0]])]});}
            var Q65;
            {var subQ0=sQuery(id+"F1.wireOp",EDGE,"E5.0.8.1");var subQ1=sQuery(id+"F1.wireOp",EDGE,"E3.7.0.0");var subQ2=makeQuery(id+"F1.imprint","INTERSECT",VERTEX,{"derivedFrom":[subQ1,subQ0]});Q65=makeQuery(id+"F1.imprint","IMPRINT",FACE,{"disambiguationData":[TD([[makeQuery(id+"F1.imprint","IMPRINT",EDGE,{"disambiguationData":[TD([[subQ2,1.0]])],"derivedFrom":subQ1}),1.0]])]});}
            var Q66;
            {var subQ0=sQuery(id+"F1.wireOp",EDGE,"E5.0.4.1");var subQ1=sQuery(id+"F1.wireOp",EDGE,"E3.3.0.1");var subQ2=makeQuery(id+"F1.imprint","INTERSECT",VERTEX,{"derivedFrom":[subQ1,subQ0]});Q66=makeQuery(id+"F1.imprint","IMPRINT",FACE,{"disambiguationData":[TD([[makeQuery(id+"F1.imprint","IMPRINT",EDGE,{"disambiguationData":[TD([[subQ2,1.0]])],"derivedFrom":subQ1}),1.0]])]});}
            var Q67;
            {var subQ0=sQuery(id+"F1.wireOp",EDGE,"E5.0.1.0");var subQ1=sQuery(id+"F1.wireOp",EDGE,"E3.2.0.1");var subQ2=makeQuery(id+"F1.imprint","INTERSECT",VERTEX,{"derivedFrom":[subQ1,subQ0]});Q67=makeQuery(id+"F1.imprint","IMPRINT",FACE,{"disambiguationData":[TD([[makeQuery(id+"F1.imprint","IMPRINT",EDGE,{"disambiguationData":[TD([[subQ2,-1.0]])],"derivedFrom":subQ1}),1.0]])]});}
            var Q68;
            {var subQ0=sQuery(id+"F1.wireOp",EDGE,"E5.0.1.1");var subQ1=sQuery(id+"F1.wireOp",EDGE,"E3.1.0.0");var subQ2=makeQuery(id+"F1.imprint","INTERSECT",VERTEX,{"derivedFrom":[subQ1,subQ0]});Q68=makeQuery(id+"F1.imprint","IMPRINT",FACE,{"disambiguationData":[TD([[makeQuery(id+"F1.imprint","IMPRINT",EDGE,{"disambiguationData":[TD([[subQ2,1.0]])],"derivedFrom":subQ1}),1.0]])]});}
            var Q69;
            {var subQ0=sQuery(id+"F1.wireOp",EDGE,"E5.0.2.1");var subQ1=sQuery(id+"F1.wireOp",EDGE,"E3.8.0.0");var subQ2=makeQuery(id+"F1.imprint","INTERSECT",VERTEX,{"derivedFrom":[subQ1,subQ0]});Q69=makeQuery(id+"F1.imprint","IMPRINT",FACE,{"disambiguationData":[TD([[makeQuery(id+"F1.imprint","IMPRINT",EDGE,{"disambiguationData":[TD([[subQ2,-1.0]])],"derivedFrom":subQ1}),1.0]])]});}
            var Q70;
            {var subQ0=sQuery(id+"F1.wireOp",EDGE,"E5.0.8.1");var subQ1=sQuery(id+"F1.wireOp",EDGE,"E3.4.0.1");var subQ2=makeQuery(id+"F1.imprint","INTERSECT",VERTEX,{"derivedFrom":[subQ1,subQ0]});Q70=makeQuery(id+"F1.imprint","IMPRINT",FACE,{"disambiguationData":[TD([[makeQuery(id+"F1.imprint","IMPRINT",EDGE,{"disambiguationData":[TD([[subQ2,1.0]])],"derivedFrom":subQ1}),1.0]])]});}
            var Q71;
            {var subQ0=sQuery(id+"F1.wireOp",EDGE,"E4.bottom");var subQ1=sQuery(id+"F1.wireOp",EDGE,"E3.7.0.1");var subQ2=makeQuery(id+"F1.imprint","INTERSECT",VERTEX,{"derivedFrom":[subQ1,subQ0]});Q71=makeQuery(id+"F1.imprint","IMPRINT",FACE,{"disambiguationData":[TD([[makeQuery(id+"F1.imprint","IMPRINT",EDGE,{"disambiguationData":[TD([[subQ2,-1.0]])],"derivedFrom":subQ1}),1.0]])]});}
            var Q72;
            {var subQ0=sQuery(id+"F1.wireOp",EDGE,"E4.bottom");var subQ1=sQuery(id+"F1.wireOp",EDGE,"E3.1.0.1");var subQ2=makeQuery(id+"F1.imprint","INTERSECT",VERTEX,{"derivedFrom":[subQ1,subQ0]});Q72=makeQuery(id+"F1.imprint","IMPRINT",FACE,{"disambiguationData":[TD([[makeQuery(id+"F1.imprint","IMPRINT",EDGE,{"disambiguationData":[TD([[subQ2,-1.0]])],"derivedFrom":subQ1}),1.0]])]});}
            var Q73;
            {var subQ0=sQuery(id+"F1.wireOp",EDGE,"E5.0.4.1");var subQ1=sQuery(id+"F1.wireOp",EDGE,"E3.1.0.0");var subQ2=makeQuery(id+"F1.imprint","INTERSECT",VERTEX,{"derivedFrom":[subQ1,subQ0]});Q73=makeQuery(id+"F1.imprint","IMPRINT",FACE,{"disambiguationData":[TD([[makeQuery(id+"F1.imprint","IMPRINT",EDGE,{"disambiguationData":[TD([[subQ2,-1.0]])],"derivedFrom":subQ1}),1.0]])]});}
            var Q74;
            {var subQ0=sQuery(id+"F1.wireOp",EDGE,"E5.0.5.0");var subQ1=sQuery(id+"F1.wireOp",EDGE,"E3.2.0.0");var subQ2=makeQuery(id+"F1.imprint","INTERSECT",VERTEX,{"derivedFrom":[subQ1,subQ0]});Q74=makeQuery(id+"F1.imprint","IMPRINT",FACE,{"disambiguationData":[TD([[makeQuery(id+"F1.imprint","IMPRINT",EDGE,{"disambiguationData":[TD([[subQ2,-1.0]])],"derivedFrom":subQ1}),1.0]])]});}
            var Q75;
            {var subQ0=sQuery(id+"F1.wireOp",EDGE,"E5.0.4.0");var subQ1=sQuery(id+"F1.wireOp",EDGE,"E3.2.0.0");var subQ2=makeQuery(id+"F1.imprint","INTERSECT",VERTEX,{"derivedFrom":[subQ1,subQ0]});Q75=makeQuery(id+"F1.imprint","IMPRINT",FACE,{"disambiguationData":[TD([[makeQuery(id+"F1.imprint","IMPRINT",EDGE,{"disambiguationData":[TD([[subQ2,1.0]])],"derivedFrom":subQ1}),1.0]])]});}
            var Q76;
            {var subQ0=sQuery(id+"F1.wireOp",EDGE,"E5.0.3.1");var subQ1=sQuery(id+"F1.wireOp",EDGE,"E3.5.0.1");var subQ2=makeQuery(id+"F1.imprint","INTERSECT",VERTEX,{"derivedFrom":[subQ1,subQ0]});Q76=makeQuery(id+"F1.imprint","IMPRINT",FACE,{"disambiguationData":[TD([[makeQuery(id+"F1.imprint","IMPRINT",EDGE,{"disambiguationData":[TD([[subQ2,1.0]])],"derivedFrom":subQ1}),1.0]])]});}
            var Q77;
            {var subQ0=sQuery(id+"F1.wireOp",EDGE,"E4.top");var subQ1=sQuery(id+"F1.wireOp",EDGE,"E3.2.0.0");var subQ2=makeQuery(id+"F1.imprint","INTERSECT",VERTEX,{"derivedFrom":[subQ1,subQ0]});Q77=makeQuery(id+"F1.imprint","IMPRINT",FACE,{"disambiguationData":[TD([[makeQuery(id+"F1.imprint","IMPRINT",EDGE,{"disambiguationData":[TD([[subQ2,-1.0]])],"derivedFrom":subQ1}),1.0]])]});}
            var Q78;
            {var subQ0=sQuery(id+"F1.wireOp",EDGE,"E5.0.3.1");var subQ1=sQuery(id+"F1.wireOp",EDGE,"E3.1.0.0");var subQ2=makeQuery(id+"F1.imprint","INTERSECT",VERTEX,{"derivedFrom":[subQ1,subQ0]});Q78=makeQuery(id+"F1.imprint","IMPRINT",FACE,{"disambiguationData":[TD([[makeQuery(id+"F1.imprint","IMPRINT",EDGE,{"disambiguationData":[TD([[subQ2,-1.0]])],"derivedFrom":subQ1}),1.0]])]});}
            var Q79;
            {var subQ0=sQuery(id+"F1.wireOp",EDGE,"E5.0.3.0");var subQ1=sQuery(id+"F1.wireOp",EDGE,"E2.left");var subQ2=makeQuery(id+"F1.imprint","INTERSECT",VERTEX,{"derivedFrom":[subQ1,subQ0]});Q79=makeQuery(id+"F1.imprint","IMPRINT",FACE,{"disambiguationData":[TD([[makeQuery(id+"F1.imprint","IMPRINT",EDGE,{"disambiguationData":[TD([[subQ2,-1.0]])],"derivedFrom":subQ1}),1.0]])]});}
            var Q80;
            {var subQ0=sQuery(id+"F1.wireOp",EDGE,"E5.0.2.0");var subQ1=sQuery(id+"F1.wireOp",EDGE,"E3.6.0.0");var subQ2=makeQuery(id+"F1.imprint","INTERSECT",VERTEX,{"derivedFrom":[subQ1,subQ0]});Q80=makeQuery(id+"F1.imprint","IMPRINT",FACE,{"disambiguationData":[TD([[makeQuery(id+"F1.imprint","IMPRINT",EDGE,{"disambiguationData":[TD([[subQ2,-1.0]])],"derivedFrom":subQ1}),1.0]])]});}
            var Q81;
            {var subQ0=sQuery(id+"F1.wireOp",EDGE,"E5.0.5.1");var subQ1=sQuery(id+"F1.wireOp",EDGE,"E3.6.0.1");var subQ2=makeQuery(id+"F1.imprint","INTERSECT",VERTEX,{"derivedFrom":[subQ1,subQ0]});Q81=makeQuery(id+"F1.imprint","IMPRINT",FACE,{"disambiguationData":[TD([[makeQuery(id+"F1.imprint","IMPRINT",EDGE,{"disambiguationData":[TD([[subQ2,1.0]])],"derivedFrom":subQ1}),1.0]])]});}
            var Q82;
            {var subQ0=sQuery(id+"F1.wireOp",EDGE,"E5.0.1.0");var subQ1=sQuery(id+"F1.wireOp",EDGE,"E3.7.0.0");var subQ2=makeQuery(id+"F1.imprint","INTERSECT",VERTEX,{"derivedFrom":[subQ1,subQ0]});Q82=makeQuery(id+"F1.imprint","IMPRINT",FACE,{"disambiguationData":[TD([[makeQuery(id+"F1.imprint","IMPRINT",EDGE,{"disambiguationData":[TD([[subQ2,-1.0]])],"derivedFrom":subQ1}),1.0]])]});}
            var Q83;
            {var subQ0=sQuery(id+"F1.wireOp",EDGE,"E5.0.7.1");var subQ1=sQuery(id+"F1.wireOp",EDGE,"E3.8.0.0");var subQ2=makeQuery(id+"F1.imprint","INTERSECT",VERTEX,{"derivedFrom":[subQ1,subQ0]});Q83=makeQuery(id+"F1.imprint","IMPRINT",FACE,{"disambiguationData":[TD([[makeQuery(id+"F1.imprint","IMPRINT",EDGE,{"disambiguationData":[TD([[subQ2,-1.0]])],"derivedFrom":subQ1}),1.0]])]});}
            var Q84;
            {var subQ0=sQuery(id+"F1.wireOp",EDGE,"E5.0.7.0");var subQ1=sQuery(id+"F1.wireOp",EDGE,"E3.6.0.1");var subQ2=makeQuery(id+"F1.imprint","INTERSECT",VERTEX,{"derivedFrom":[subQ1,subQ0]});Q84=makeQuery(id+"F1.imprint","IMPRINT",FACE,{"disambiguationData":[TD([[makeQuery(id+"F1.imprint","IMPRINT",EDGE,{"disambiguationData":[TD([[subQ2,-1.0]])],"derivedFrom":subQ1}),1.0]])]});}
            var Q85;
            {var subQ0=sQuery(id+"F1.wireOp",EDGE,"E5.0.3.1");var subQ1=sQuery(id+"F1.wireOp",EDGE,"E3.5.0.0");var subQ2=makeQuery(id+"F1.imprint","INTERSECT",VERTEX,{"derivedFrom":[subQ1,subQ0]});Q85=makeQuery(id+"F1.imprint","IMPRINT",FACE,{"disambiguationData":[TD([[makeQuery(id+"F1.imprint","IMPRINT",EDGE,{"disambiguationData":[TD([[subQ2,1.0]])],"derivedFrom":subQ1}),1.0]])]});}
            var Q86;
            {var subQ0=sQuery(id+"F1.wireOp",EDGE,"E5.0.4.1");var subQ1=sQuery(id+"F1.wireOp",EDGE,"E3.4.0.1");var subQ2=makeQuery(id+"F1.imprint","INTERSECT",VERTEX,{"derivedFrom":[subQ1,subQ0]});Q86=makeQuery(id+"F1.imprint","IMPRINT",FACE,{"disambiguationData":[TD([[makeQuery(id+"F1.imprint","IMPRINT",EDGE,{"disambiguationData":[TD([[subQ2,1.0]])],"derivedFrom":subQ1}),1.0]])]});}
            var Q87;
            {var subQ0=sQuery(id+"F1.wireOp",EDGE,"E4.bottom");var subQ1=sQuery(id+"F1.wireOp",EDGE,"E3.7.0.0");var subQ2=makeQuery(id+"F1.imprint","INTERSECT",VERTEX,{"derivedFrom":[subQ1,subQ0]});Q87=makeQuery(id+"F1.imprint","IMPRINT",FACE,{"disambiguationData":[TD([[makeQuery(id+"F1.imprint","IMPRINT",EDGE,{"disambiguationData":[TD([[subQ2,-1.0]])],"derivedFrom":subQ1}),1.0]])]});}
            var Q88;
            {var subQ0=sQuery(id+"F1.wireOp",EDGE,"E5.0.4.0");var subQ1=sQuery(id+"F1.wireOp",EDGE,"E3.2.0.1");var subQ2=makeQuery(id+"F1.imprint","INTERSECT",VERTEX,{"derivedFrom":[subQ1,subQ0]});Q88=makeQuery(id+"F1.imprint","IMPRINT",FACE,{"disambiguationData":[TD([[makeQuery(id+"F1.imprint","IMPRINT",EDGE,{"disambiguationData":[TD([[subQ2,-1.0]])],"derivedFrom":subQ1}),1.0]])]});}
            var Q89;
            {var subQ0=sQuery(id+"F1.wireOp",EDGE,"E5.0.5.0");var subQ1=sQuery(id+"F1.wireOp",EDGE,"E3.8.0.0");var subQ2=makeQuery(id+"F1.imprint","INTERSECT",VERTEX,{"derivedFrom":[subQ1,subQ0]});Q89=makeQuery(id+"F1.imprint","IMPRINT",FACE,{"disambiguationData":[TD([[makeQuery(id+"F1.imprint","IMPRINT",EDGE,{"disambiguationData":[TD([[subQ2,-1.0]])],"derivedFrom":subQ1}),1.0]])]});}
            var Q90;
            {var subQ0=sQuery(id+"F1.wireOp",EDGE,"E5.0.3.1");var subQ1=sQuery(id+"F1.wireOp",EDGE,"E3.4.0.0");var subQ2=makeQuery(id+"F1.imprint","INTERSECT",VERTEX,{"derivedFrom":[subQ1,subQ0]});Q90=makeQuery(id+"F1.imprint","IMPRINT",FACE,{"disambiguationData":[TD([[makeQuery(id+"F1.imprint","IMPRINT",EDGE,{"disambiguationData":[TD([[subQ2,-1.0]])],"derivedFrom":subQ1}),1.0]])]});}
            var Q91;
            {var subQ0=sQuery(id+"F1.wireOp",EDGE,"E5.0.8.1");var subQ1=sQuery(id+"F1.wireOp",EDGE,"E3.5.0.1");var subQ2=makeQuery(id+"F1.imprint","INTERSECT",VERTEX,{"derivedFrom":[subQ1,subQ0]});Q91=makeQuery(id+"F1.imprint","IMPRINT",FACE,{"disambiguationData":[TD([[makeQuery(id+"F1.imprint","IMPRINT",EDGE,{"disambiguationData":[TD([[subQ2,1.0]])],"derivedFrom":subQ1}),1.0]])]});}
            var Q92;
            {var subQ0=sQuery(id+"F1.wireOp",EDGE,"E5.0.1.1");var subQ1=sQuery(id+"F1.wireOp",EDGE,"E3.7.0.0");var subQ2=makeQuery(id+"F1.imprint","INTERSECT",VERTEX,{"derivedFrom":[subQ1,subQ0]});Q92=makeQuery(id+"F1.imprint","IMPRINT",FACE,{"disambiguationData":[TD([[makeQuery(id+"F1.imprint","IMPRINT",EDGE,{"disambiguationData":[TD([[subQ2,-1.0]])],"derivedFrom":subQ1}),1.0]])]});}
            var Q93;
            {var subQ0=sQuery(id+"F1.wireOp",EDGE,"E5.0.4.0");var subQ1=sQuery(id+"F1.wireOp",EDGE,"E3.3.0.0");var subQ2=makeQuery(id+"F1.imprint","INTERSECT",VERTEX,{"derivedFrom":[subQ1,subQ0]});Q93=makeQuery(id+"F1.imprint","IMPRINT",FACE,{"disambiguationData":[TD([[makeQuery(id+"F1.imprint","IMPRINT",EDGE,{"disambiguationData":[TD([[subQ2,-1.0]])],"derivedFrom":subQ1}),1.0]])]});}
            var Q94;
            {var subQ0=sQuery(id+"F1.wireOp",EDGE,"E5.0.5.0");var subQ1=sQuery(id+"F1.wireOp",EDGE,"E3.3.0.0");var subQ2=makeQuery(id+"F1.imprint","INTERSECT",VERTEX,{"derivedFrom":[subQ1,subQ0]});Q94=makeQuery(id+"F1.imprint","IMPRINT",FACE,{"disambiguationData":[TD([[makeQuery(id+"F1.imprint","IMPRINT",EDGE,{"disambiguationData":[TD([[subQ2,1.0]])],"derivedFrom":subQ1}),1.0]])]});}
            var Q95;
            {var subQ0=sQuery(id+"F1.wireOp",EDGE,"E5.0.2.1");var subQ1=sQuery(id+"F1.wireOp",EDGE,"E3.5.0.1");var subQ2=makeQuery(id+"F1.imprint","INTERSECT",VERTEX,{"derivedFrom":[subQ1,subQ0]});Q95=makeQuery(id+"F1.imprint","IMPRINT",FACE,{"disambiguationData":[TD([[makeQuery(id+"F1.imprint","IMPRINT",EDGE,{"disambiguationData":[TD([[subQ2,1.0]])],"derivedFrom":subQ1}),1.0]])]});}
            var Q96;
            {var subQ0=sQuery(id+"F1.wireOp",EDGE,"E5.0.2.1");var subQ1=sQuery(id+"F1.wireOp",EDGE,"E3.4.0.0");var subQ2=makeQuery(id+"F1.imprint","INTERSECT",VERTEX,{"derivedFrom":[subQ1,subQ0]});Q96=makeQuery(id+"F1.imprint","IMPRINT",FACE,{"disambiguationData":[TD([[makeQuery(id+"F1.imprint","IMPRINT",EDGE,{"disambiguationData":[TD([[subQ2,1.0]])],"derivedFrom":subQ1}),1.0]])]});}
            var Q97;
            {var subQ0=sQuery(id+"F1.wireOp",EDGE,"E5.0.2.1");var subQ1=sQuery(id+"F1.wireOp",EDGE,"E3.6.0.1");var subQ2=makeQuery(id+"F1.imprint","INTERSECT",VERTEX,{"derivedFrom":[subQ1,subQ0]});Q97=makeQuery(id+"F1.imprint","IMPRINT",FACE,{"disambiguationData":[TD([[makeQuery(id+"F1.imprint","IMPRINT",EDGE,{"disambiguationData":[TD([[subQ2,1.0]])],"derivedFrom":subQ1}),1.0]])]});}
            var Q98;
            {var subQ0=sQuery(id+"F1.wireOp",EDGE,"E5.0.5.0");var subQ1=sQuery(id+"F1.wireOp",EDGE,"E3.6.0.0");var subQ2=makeQuery(id+"F1.imprint","INTERSECT",VERTEX,{"derivedFrom":[subQ1,subQ0]});Q98=makeQuery(id+"F1.imprint","IMPRINT",FACE,{"disambiguationData":[TD([[makeQuery(id+"F1.imprint","IMPRINT",EDGE,{"disambiguationData":[TD([[subQ2,-1.0]])],"derivedFrom":subQ1}),1.0]])]});}
            var Q99;
            {var subQ0=sQuery(id+"F1.wireOp",EDGE,"E5.0.6.1");var subQ1=sQuery(id+"F1.wireOp",EDGE,"E3.4.0.1");var subQ2=makeQuery(id+"F1.imprint","INTERSECT",VERTEX,{"derivedFrom":[subQ1,subQ0]});Q99=makeQuery(id+"F1.imprint","IMPRINT",FACE,{"disambiguationData":[TD([[makeQuery(id+"F1.imprint","IMPRINT",EDGE,{"disambiguationData":[TD([[subQ2,1.0]])],"derivedFrom":subQ1}),1.0]])]});}
            var Q100;
            {var subQ0=sQuery(id+"F1.wireOp",EDGE,"E5.0.3.1");var subQ1=sQuery(id+"F1.wireOp",EDGE,"E3.1.0.1");var subQ2=makeQuery(id+"F1.imprint","INTERSECT",VERTEX,{"derivedFrom":[subQ1,subQ0]});Q100=makeQuery(id+"F1.imprint","IMPRINT",FACE,{"disambiguationData":[TD([[makeQuery(id+"F1.imprint","IMPRINT",EDGE,{"disambiguationData":[TD([[subQ2,1.0]])],"derivedFrom":subQ1}),1.0]])]});}
            var Q101;
            {var subQ0=sQuery(id+"F1.wireOp",EDGE,"E5.0.3.0");var subQ1=sQuery(id+"F1.wireOp",EDGE,"E3.6.0.1");var subQ2=makeQuery(id+"F1.imprint","INTERSECT",VERTEX,{"derivedFrom":[subQ1,subQ0]});Q101=makeQuery(id+"F1.imprint","IMPRINT",FACE,{"disambiguationData":[TD([[makeQuery(id+"F1.imprint","IMPRINT",EDGE,{"disambiguationData":[TD([[subQ2,-1.0]])],"derivedFrom":subQ1}),1.0]])]});}
            var Q102;
            {var subQ0=sQuery(id+"F1.wireOp",EDGE,"E4.bottom");var subQ1=sQuery(id+"F1.wireOp",EDGE,"E3.2.0.1");var subQ2=makeQuery(id+"F1.imprint","INTERSECT",VERTEX,{"derivedFrom":[subQ1,subQ0]});Q102=makeQuery(id+"F1.imprint","IMPRINT",FACE,{"disambiguationData":[TD([[makeQuery(id+"F1.imprint","IMPRINT",EDGE,{"disambiguationData":[TD([[subQ2,-1.0]])],"derivedFrom":subQ1}),1.0]])]});}
            var Q103;
            {var subQ0=sQuery(id+"F1.wireOp",EDGE,"E5.0.6.1");var subQ1=sQuery(id+"F1.wireOp",EDGE,"E3.3.0.0");var subQ2=makeQuery(id+"F1.imprint","INTERSECT",VERTEX,{"derivedFrom":[subQ1,subQ0]});Q103=makeQuery(id+"F1.imprint","IMPRINT",FACE,{"disambiguationData":[TD([[makeQuery(id+"F1.imprint","IMPRINT",EDGE,{"disambiguationData":[TD([[subQ2,1.0]])],"derivedFrom":subQ1}),1.0]])]});}
            var Q104;
            {var subQ0=sQuery(id+"F1.wireOp",EDGE,"E5.0.6.1");var subQ1=sQuery(id+"F1.wireOp",EDGE,"E3.3.0.1");var subQ2=makeQuery(id+"F1.imprint","INTERSECT",VERTEX,{"derivedFrom":[subQ1,subQ0]});Q104=makeQuery(id+"F1.imprint","IMPRINT",FACE,{"disambiguationData":[TD([[makeQuery(id+"F1.imprint","IMPRINT",EDGE,{"disambiguationData":[TD([[subQ2,1.0]])],"derivedFrom":subQ1}),1.0]])]});}
            var Q105;
            {var subQ0=sQuery(id+"F1.wireOp",EDGE,"E5.0.5.0");var subQ1=sQuery(id+"F1.wireOp",EDGE,"E2.left");var subQ2=makeQuery(id+"F1.imprint","INTERSECT",VERTEX,{"derivedFrom":[subQ1,subQ0]});Q105=makeQuery(id+"F1.imprint","IMPRINT",FACE,{"disambiguationData":[TD([[makeQuery(id+"F1.imprint","IMPRINT",EDGE,{"disambiguationData":[TD([[subQ2,-1.0]])],"derivedFrom":subQ1}),1.0]])]});}
            var Q106;
            {var subQ0=sQuery(id+"F1.wireOp",EDGE,"E4.bottom");var subQ1=sQuery(id+"F1.wireOp",EDGE,"E2.left");var subQ2=makeQuery(id+"F1.imprint","INTERSECT",VERTEX,{"derivedFrom":[subQ1,subQ0]});Q106=makeQuery(id+"F1.imprint","IMPRINT",FACE,{"disambiguationData":[TD([[makeQuery(id+"F1.imprint","IMPRINT",EDGE,{"disambiguationData":[TD([[subQ2,-1.0]])],"derivedFrom":subQ1}),1.0]])]});}
            var Q107;
            {var subQ0=sQuery(id+"F1.wireOp",EDGE,"E5.0.8.1");var subQ1=sQuery(id+"F1.wireOp",EDGE,"E3.1.0.0");var subQ2=makeQuery(id+"F1.imprint","INTERSECT",VERTEX,{"derivedFrom":[subQ1,subQ0]});Q107=makeQuery(id+"F1.imprint","IMPRINT",FACE,{"disambiguationData":[TD([[makeQuery(id+"F1.imprint","IMPRINT",EDGE,{"disambiguationData":[TD([[subQ2,1.0]])],"derivedFrom":subQ1}),1.0]])]});}
            var Q108;
            {var subQ0=sQuery(id+"F1.wireOp",EDGE,"E5.0.2.0");var subQ1=sQuery(id+"F1.wireOp",EDGE,"E3.1.0.1");var subQ2=makeQuery(id+"F1.imprint","INTERSECT",VERTEX,{"derivedFrom":[subQ1,subQ0]});Q108=makeQuery(id+"F1.imprint","IMPRINT",FACE,{"disambiguationData":[TD([[makeQuery(id+"F1.imprint","IMPRINT",EDGE,{"disambiguationData":[TD([[subQ2,-1.0]])],"derivedFrom":subQ1}),1.0]])]});}
            var Q109;
            {var subQ0=sQuery(id+"F1.wireOp",EDGE,"E5.0.2.0");var subQ1=sQuery(id+"F1.wireOp",EDGE,"E3.2.0.0");var subQ2=makeQuery(id+"F1.imprint","INTERSECT",VERTEX,{"derivedFrom":[subQ1,subQ0]});Q109=makeQuery(id+"F1.imprint","IMPRINT",FACE,{"disambiguationData":[TD([[makeQuery(id+"F1.imprint","IMPRINT",EDGE,{"disambiguationData":[TD([[subQ2,-1.0]])],"derivedFrom":subQ1}),1.0]])]});}
            var Q110;
            {var subQ0=sQuery(id+"F1.wireOp",EDGE,"E5.0.3.1");var subQ1=sQuery(id+"F1.wireOp",EDGE,"E3.7.0.1");var subQ2=makeQuery(id+"F1.imprint","INTERSECT",VERTEX,{"derivedFrom":[subQ1,subQ0]});Q110=makeQuery(id+"F1.imprint","IMPRINT",FACE,{"disambiguationData":[TD([[makeQuery(id+"F1.imprint","IMPRINT",EDGE,{"disambiguationData":[TD([[subQ2,1.0]])],"derivedFrom":subQ1}),1.0]])]});}
            var Q111;
            {var subQ0=sQuery(id+"F1.wireOp",EDGE,"E5.0.1.1");var subQ1=sQuery(id+"F1.wireOp",EDGE,"E3.6.0.0");var subQ2=makeQuery(id+"F1.imprint","INTERSECT",VERTEX,{"derivedFrom":[subQ1,subQ0]});Q111=makeQuery(id+"F1.imprint","IMPRINT",FACE,{"disambiguationData":[TD([[makeQuery(id+"F1.imprint","IMPRINT",EDGE,{"disambiguationData":[TD([[subQ2,1.0]])],"derivedFrom":subQ1}),1.0]])]});}
            var Q112;
            {var subQ0=sQuery(id+"F1.wireOp",EDGE,"E5.0.2.0");var subQ1=sQuery(id+"F1.wireOp",EDGE,"E3.6.0.0");var subQ2=makeQuery(id+"F1.imprint","INTERSECT",VERTEX,{"derivedFrom":[subQ1,subQ0]});Q112=makeQuery(id+"F1.imprint","IMPRINT",FACE,{"disambiguationData":[TD([[makeQuery(id+"F1.imprint","IMPRINT",EDGE,{"disambiguationData":[TD([[subQ2,1.0]])],"derivedFrom":subQ1}),1.0]])]});}
            var Q113;
            {var subQ0=sQuery(id+"F1.wireOp",EDGE,"E5.0.3.0");var subQ1=sQuery(id+"F1.wireOp",EDGE,"E3.4.0.0");var subQ2=makeQuery(id+"F1.imprint","INTERSECT",VERTEX,{"derivedFrom":[subQ1,subQ0]});Q113=makeQuery(id+"F1.imprint","IMPRINT",FACE,{"disambiguationData":[TD([[makeQuery(id+"F1.imprint","IMPRINT",EDGE,{"disambiguationData":[TD([[subQ2,1.0]])],"derivedFrom":subQ1}),1.0]])]});}
            var Q114;
            {var subQ0=sQuery(id+"F1.wireOp",EDGE,"E5.0.6.1");var subQ1=sQuery(id+"F1.wireOp",EDGE,"E3.5.0.0");var subQ2=makeQuery(id+"F1.imprint","INTERSECT",VERTEX,{"derivedFrom":[subQ1,subQ0]});Q114=makeQuery(id+"F1.imprint","IMPRINT",FACE,{"disambiguationData":[TD([[makeQuery(id+"F1.imprint","IMPRINT",EDGE,{"disambiguationData":[TD([[subQ2,-1.0]])],"derivedFrom":subQ1}),1.0]])]});}
            var Q115;
            {var subQ0=sQuery(id+"F1.wireOp",EDGE,"E5.0.5.0");var subQ1=sQuery(id+"F1.wireOp",EDGE,"E3.2.0.0");var subQ2=makeQuery(id+"F1.imprint","INTERSECT",VERTEX,{"derivedFrom":[subQ1,subQ0]});Q115=makeQuery(id+"F1.imprint","IMPRINT",FACE,{"disambiguationData":[TD([[makeQuery(id+"F1.imprint","IMPRINT",EDGE,{"disambiguationData":[TD([[subQ2,1.0]])],"derivedFrom":subQ1}),1.0]])]});}
            var Q116;
            {var subQ0=sQuery(id+"F1.wireOp",EDGE,"E5.0.7.0");var subQ1=sQuery(id+"F1.wireOp",EDGE,"E2.left");var subQ2=makeQuery(id+"F1.imprint","INTERSECT",VERTEX,{"derivedFrom":[subQ1,subQ0]});Q116=makeQuery(id+"F1.imprint","IMPRINT",FACE,{"disambiguationData":[TD([[makeQuery(id+"F1.imprint","IMPRINT",EDGE,{"disambiguationData":[TD([[subQ2,-1.0]])],"derivedFrom":subQ1}),1.0]])]});}
            var Q117;
            {var subQ0=sQuery(id+"F1.wireOp",EDGE,"E5.0.3.1");var subQ1=sQuery(id+"F1.wireOp",EDGE,"E3.2.0.1");var subQ2=makeQuery(id+"F1.imprint","INTERSECT",VERTEX,{"derivedFrom":[subQ1,subQ0]});Q117=makeQuery(id+"F1.imprint","IMPRINT",FACE,{"disambiguationData":[TD([[makeQuery(id+"F1.imprint","IMPRINT",EDGE,{"disambiguationData":[TD([[subQ2,1.0]])],"derivedFrom":subQ1}),1.0]])]});}
            var Q118;
            {var subQ0=sQuery(id+"F1.wireOp",EDGE,"E5.0.4.0");var subQ1=sQuery(id+"F1.wireOp",EDGE,"E3.2.0.0");var subQ2=makeQuery(id+"F1.imprint","INTERSECT",VERTEX,{"derivedFrom":[subQ1,subQ0]});Q118=makeQuery(id+"F1.imprint","IMPRINT",FACE,{"disambiguationData":[TD([[makeQuery(id+"F1.imprint","IMPRINT",EDGE,{"disambiguationData":[TD([[subQ2,-1.0]])],"derivedFrom":subQ1}),1.0]])]});}
            var Q119;
            {var subQ0=sQuery(id+"F1.wireOp",EDGE,"E5.0.1.0");var subQ1=sQuery(id+"F1.wireOp",EDGE,"E3.7.0.0");var subQ2=makeQuery(id+"F1.imprint","INTERSECT",VERTEX,{"derivedFrom":[subQ1,subQ0]});Q119=makeQuery(id+"F1.imprint","IMPRINT",FACE,{"disambiguationData":[TD([[makeQuery(id+"F1.imprint","IMPRINT",EDGE,{"disambiguationData":[TD([[subQ2,1.0]])],"derivedFrom":subQ1}),1.0]])]});}
            var Q120;
            {var subQ0=sQuery(id+"F1.wireOp",EDGE,"E5.0.6.1");var subQ1=sQuery(id+"F1.wireOp",EDGE,"E3.1.0.1");var subQ2=makeQuery(id+"F1.imprint","INTERSECT",VERTEX,{"derivedFrom":[subQ1,subQ0]});Q120=makeQuery(id+"F1.imprint","IMPRINT",FACE,{"disambiguationData":[TD([[makeQuery(id+"F1.imprint","IMPRINT",EDGE,{"disambiguationData":[TD([[subQ2,1.0]])],"derivedFrom":subQ1}),1.0]])]});}
            var Q121;
            {var subQ0=sQuery(id+"F1.wireOp",EDGE,"E5.0.2.1");var subQ1=sQuery(id+"F1.wireOp",EDGE,"E2.left");var subQ2=makeQuery(id+"F1.imprint","INTERSECT",VERTEX,{"derivedFrom":[subQ1,subQ0]});Q121=makeQuery(id+"F1.imprint","IMPRINT",FACE,{"disambiguationData":[TD([[makeQuery(id+"F1.imprint","IMPRINT",EDGE,{"disambiguationData":[TD([[subQ2,1.0]])],"derivedFrom":subQ1}),1.0]])]});}
            var Q122;
            {var subQ0=sQuery(id+"F1.wireOp",EDGE,"E5.0.8.1");var subQ1=sQuery(id+"F1.wireOp",EDGE,"E3.2.0.0");var subQ2=makeQuery(id+"F1.imprint","INTERSECT",VERTEX,{"derivedFrom":[subQ1,subQ0]});Q122=makeQuery(id+"F1.imprint","IMPRINT",FACE,{"disambiguationData":[TD([[makeQuery(id+"F1.imprint","IMPRINT",EDGE,{"disambiguationData":[TD([[subQ2,1.0]])],"derivedFrom":subQ1}),1.0]])]});}
            var Q123;
            {var subQ0=sQuery(id+"F1.wireOp",EDGE,"E5.0.3.1");var subQ1=sQuery(id+"F1.wireOp",EDGE,"E3.2.0.0");var subQ2=makeQuery(id+"F1.imprint","INTERSECT",VERTEX,{"derivedFrom":[subQ1,subQ0]});Q123=makeQuery(id+"F1.imprint","IMPRINT",FACE,{"disambiguationData":[TD([[makeQuery(id+"F1.imprint","IMPRINT",EDGE,{"disambiguationData":[TD([[subQ2,1.0]])],"derivedFrom":subQ1}),1.0]])]});}
            var Q124;
            {var subQ0=sQuery(id+"F1.wireOp",EDGE,"E5.0.2.0");var subQ1=sQuery(id+"F1.wireOp",EDGE,"E3.2.0.1");var subQ2=makeQuery(id+"F1.imprint","INTERSECT",VERTEX,{"derivedFrom":[subQ1,subQ0]});Q124=makeQuery(id+"F1.imprint","IMPRINT",FACE,{"disambiguationData":[TD([[makeQuery(id+"F1.imprint","IMPRINT",EDGE,{"disambiguationData":[TD([[subQ2,-1.0]])],"derivedFrom":subQ1}),1.0]])]});}
            var Q125;
            {var subQ0=sQuery(id+"F1.wireOp",EDGE,"E5.0.7.1");var subQ1=sQuery(id+"F1.wireOp",EDGE,"E3.3.0.0");var subQ2=makeQuery(id+"F1.imprint","INTERSECT",VERTEX,{"derivedFrom":[subQ1,subQ0]});Q125=makeQuery(id+"F1.imprint","IMPRINT",FACE,{"disambiguationData":[TD([[makeQuery(id+"F1.imprint","IMPRINT",EDGE,{"disambiguationData":[TD([[subQ2,1.0]])],"derivedFrom":subQ1}),1.0]])]});}
            var Q126;
            {var subQ0=sQuery(id+"F1.wireOp",EDGE,"E5.0.7.1");var subQ1=sQuery(id+"F1.wireOp",EDGE,"E3.4.0.0");var subQ2=makeQuery(id+"F1.imprint","INTERSECT",VERTEX,{"derivedFrom":[subQ1,subQ0]});Q126=makeQuery(id+"F1.imprint","IMPRINT",FACE,{"disambiguationData":[TD([[makeQuery(id+"F1.imprint","IMPRINT",EDGE,{"disambiguationData":[TD([[subQ2,-1.0]])],"derivedFrom":subQ1}),1.0]])]});}
            var Q127;
            {var subQ0=sQuery(id+"F1.wireOp",EDGE,"E5.0.2.0");var subQ1=sQuery(id+"F1.wireOp",EDGE,"E3.5.0.0");var subQ2=makeQuery(id+"F1.imprint","INTERSECT",VERTEX,{"derivedFrom":[subQ1,subQ0]});Q127=makeQuery(id+"F1.imprint","IMPRINT",FACE,{"disambiguationData":[TD([[makeQuery(id+"F1.imprint","IMPRINT",EDGE,{"disambiguationData":[TD([[subQ2,1.0]])],"derivedFrom":subQ1}),1.0]])]});}
            var Q128;
            {var subQ0=sQuery(id+"F1.wireOp",EDGE,"E5.0.2.0");var subQ1=sQuery(id+"F1.wireOp",EDGE,"E2.right");var subQ2=makeQuery(id+"F1.imprint","INTERSECT",VERTEX,{"derivedFrom":[subQ1,subQ0]});Q128=makeQuery(id+"F1.imprint","IMPRINT",FACE,{"disambiguationData":[TD([[makeQuery(id+"F1.imprint","IMPRINT",EDGE,{"disambiguationData":[TD([[subQ2,-1.0]])],"derivedFrom":subQ1}),1.0]])]});}
            var Q129;
            {var subQ0=sQuery(id+"F1.wireOp",EDGE,"E5.0.7.0");var subQ1=sQuery(id+"F1.wireOp",EDGE,"E3.4.0.0");var subQ2=makeQuery(id+"F1.imprint","INTERSECT",VERTEX,{"derivedFrom":[subQ1,subQ0]});Q129=makeQuery(id+"F1.imprint","IMPRINT",FACE,{"disambiguationData":[TD([[makeQuery(id+"F1.imprint","IMPRINT",EDGE,{"disambiguationData":[TD([[subQ2,-1.0]])],"derivedFrom":subQ1}),1.0]])]});}
            var Q130;
            {var subQ0=sQuery(id+"F1.wireOp",EDGE,"E5.0.8.1");var subQ1=sQuery(id+"F1.wireOp",EDGE,"E2.left");var subQ2=makeQuery(id+"F1.imprint","INTERSECT",VERTEX,{"derivedFrom":[subQ1,subQ0]});Q130=makeQuery(id+"F1.imprint","IMPRINT",FACE,{"disambiguationData":[TD([[makeQuery(id+"F1.imprint","IMPRINT",EDGE,{"disambiguationData":[TD([[subQ2,1.0]])],"derivedFrom":subQ1}),1.0]])]});}
            var Q131;
            {var subQ0=sQuery(id+"F1.wireOp",EDGE,"E5.0.6.1");var subQ1=sQuery(id+"F1.wireOp",EDGE,"E2.left");var subQ2=makeQuery(id+"F1.imprint","INTERSECT",VERTEX,{"derivedFrom":[subQ1,subQ0]});Q131=makeQuery(id+"F1.imprint","IMPRINT",FACE,{"disambiguationData":[TD([[makeQuery(id+"F1.imprint","IMPRINT",EDGE,{"disambiguationData":[TD([[subQ2,1.0]])],"derivedFrom":subQ1}),1.0]])]});}
            var Q132;
            {var subQ0=sQuery(id+"F1.wireOp",EDGE,"E5.0.7.0");var subQ1=sQuery(id+"F1.wireOp",EDGE,"E3.6.0.0");var subQ2=makeQuery(id+"F1.imprint","INTERSECT",VERTEX,{"derivedFrom":[subQ1,subQ0]});Q132=makeQuery(id+"F1.imprint","IMPRINT",FACE,{"disambiguationData":[TD([[makeQuery(id+"F1.imprint","IMPRINT",EDGE,{"disambiguationData":[TD([[subQ2,-1.0]])],"derivedFrom":subQ1}),1.0]])]});}
            var Q133;
            {var subQ0=sQuery(id+"F1.wireOp",EDGE,"E5.0.2.0");var subQ1=sQuery(id+"F1.wireOp",EDGE,"E3.8.0.0");var subQ2=makeQuery(id+"F1.imprint","INTERSECT",VERTEX,{"derivedFrom":[subQ1,subQ0]});Q133=makeQuery(id+"F1.imprint","IMPRINT",FACE,{"disambiguationData":[TD([[makeQuery(id+"F1.imprint","IMPRINT",EDGE,{"disambiguationData":[TD([[subQ2,-1.0]])],"derivedFrom":subQ1}),1.0]])]});}
            var Q134;
            {var subQ0=sQuery(id+"F1.wireOp",EDGE,"E5.0.3.1");var subQ1=sQuery(id+"F1.wireOp",EDGE,"E2.left");var subQ2=makeQuery(id+"F1.imprint","INTERSECT",VERTEX,{"derivedFrom":[subQ1,subQ0]});Q134=makeQuery(id+"F1.imprint","IMPRINT",FACE,{"disambiguationData":[TD([[makeQuery(id+"F1.imprint","IMPRINT",EDGE,{"disambiguationData":[TD([[subQ2,-1.0]])],"derivedFrom":subQ1}),1.0]])]});}
            var Q135;
            {var subQ0=sQuery(id+"F1.wireOp",EDGE,"E5.0.5.0");var subQ1=sQuery(id+"F1.wireOp",EDGE,"E3.5.0.0");var subQ2=makeQuery(id+"F1.imprint","INTERSECT",VERTEX,{"derivedFrom":[subQ1,subQ0]});Q135=makeQuery(id+"F1.imprint","IMPRINT",FACE,{"disambiguationData":[TD([[makeQuery(id+"F1.imprint","IMPRINT",EDGE,{"disambiguationData":[TD([[subQ2,-1.0]])],"derivedFrom":subQ1}),1.0]])]});}
            var Q136;
            {var subQ0=sQuery(id+"F1.wireOp",EDGE,"E4.bottom");var subQ1=sQuery(id+"F1.wireOp",EDGE,"E3.1.0.0");var subQ2=makeQuery(id+"F1.imprint","INTERSECT",VERTEX,{"derivedFrom":[subQ1,subQ0]});Q136=makeQuery(id+"F1.imprint","IMPRINT",FACE,{"disambiguationData":[TD([[makeQuery(id+"F1.imprint","IMPRINT",EDGE,{"disambiguationData":[TD([[subQ2,-1.0]])],"derivedFrom":subQ1}),1.0]])]});}
            var Q137;
            {var subQ0=sQuery(id+"F1.wireOp",EDGE,"E5.0.2.1");var subQ1=sQuery(id+"F1.wireOp",EDGE,"E3.7.0.0");var subQ2=makeQuery(id+"F1.imprint","INTERSECT",VERTEX,{"derivedFrom":[subQ1,subQ0]});Q137=makeQuery(id+"F1.imprint","IMPRINT",FACE,{"disambiguationData":[TD([[makeQuery(id+"F1.imprint","IMPRINT",EDGE,{"disambiguationData":[TD([[subQ2,-1.0]])],"derivedFrom":subQ1}),1.0]])]});}
            var Q138;
            {var subQ0=sQuery(id+"F1.wireOp",EDGE,"E5.0.1.0");var subQ1=sQuery(id+"F1.wireOp",EDGE,"E3.2.0.0");var subQ2=makeQuery(id+"F1.imprint","INTERSECT",VERTEX,{"derivedFrom":[subQ1,subQ0]});Q138=makeQuery(id+"F1.imprint","IMPRINT",FACE,{"disambiguationData":[TD([[makeQuery(id+"F1.imprint","IMPRINT",EDGE,{"disambiguationData":[TD([[subQ2,-1.0]])],"derivedFrom":subQ1}),1.0]])]});}
            var Q139;
            {var subQ0=sQuery(id+"F1.wireOp",EDGE,"E5.0.8.0");var subQ1=sQuery(id+"F1.wireOp",EDGE,"E2.left");var subQ2=makeQuery(id+"F1.imprint","INTERSECT",VERTEX,{"derivedFrom":[subQ1,subQ0]});Q139=makeQuery(id+"F1.imprint","IMPRINT",FACE,{"disambiguationData":[TD([[makeQuery(id+"F1.imprint","IMPRINT",EDGE,{"disambiguationData":[TD([[subQ2,1.0]])],"derivedFrom":subQ1}),1.0]])]});}
            var Q140;
            {var subQ0=sQuery(id+"F1.wireOp",EDGE,"E5.0.7.0");var subQ1=sQuery(id+"F1.wireOp",EDGE,"E2.left");var subQ2=makeQuery(id+"F1.imprint","INTERSECT",VERTEX,{"derivedFrom":[subQ1,subQ0]});Q140=makeQuery(id+"F1.imprint","IMPRINT",FACE,{"disambiguationData":[TD([[makeQuery(id+"F1.imprint","IMPRINT",EDGE,{"disambiguationData":[TD([[subQ2,1.0]])],"derivedFrom":subQ1}),1.0]])]});}
            var Q141;
            {var subQ0=sQuery(id+"F1.wireOp",EDGE,"E5.0.1.0");var subQ1=sQuery(id+"F1.wireOp",EDGE,"E3.7.0.1");var subQ2=makeQuery(id+"F1.imprint","INTERSECT",VERTEX,{"derivedFrom":[subQ1,subQ0]});Q141=makeQuery(id+"F1.imprint","IMPRINT",FACE,{"disambiguationData":[TD([[makeQuery(id+"F1.imprint","IMPRINT",EDGE,{"disambiguationData":[TD([[subQ2,-1.0]])],"derivedFrom":subQ1}),1.0]])]});}
            var Q142;
            {var subQ0=sQuery(id+"F1.wireOp",EDGE,"E5.0.7.1");var subQ1=sQuery(id+"F1.wireOp",EDGE,"E3.2.0.1");var subQ2=makeQuery(id+"F1.imprint","INTERSECT",VERTEX,{"derivedFrom":[subQ1,subQ0]});Q142=makeQuery(id+"F1.imprint","IMPRINT",FACE,{"disambiguationData":[TD([[makeQuery(id+"F1.imprint","IMPRINT",EDGE,{"disambiguationData":[TD([[subQ2,1.0]])],"derivedFrom":subQ1}),1.0]])]});}
            var Q143;
            {var subQ0=sQuery(id+"F1.wireOp",EDGE,"E5.0.1.1");var subQ1=sQuery(id+"F1.wireOp",EDGE,"E3.1.0.0");var subQ2=makeQuery(id+"F1.imprint","INTERSECT",VERTEX,{"derivedFrom":[subQ1,subQ0]});Q143=makeQuery(id+"F1.imprint","IMPRINT",FACE,{"disambiguationData":[TD([[makeQuery(id+"F1.imprint","IMPRINT",EDGE,{"disambiguationData":[TD([[subQ2,-1.0]])],"derivedFrom":subQ1}),1.0]])]});}
            var Q144;
            {var subQ0=sQuery(id+"F1.wireOp",EDGE,"E4.top");var subQ1=sQuery(id+"F1.wireOp",EDGE,"E3.5.0.0");var subQ2=makeQuery(id+"F1.imprint","INTERSECT",VERTEX,{"derivedFrom":[subQ1,subQ0]});Q144=makeQuery(id+"F1.imprint","IMPRINT",FACE,{"disambiguationData":[TD([[makeQuery(id+"F1.imprint","IMPRINT",EDGE,{"disambiguationData":[TD([[subQ2,1.0]])],"derivedFrom":subQ1}),1.0]])]});}
            var Q145;
            {var subQ0=sQuery(id+"F1.wireOp",EDGE,"E5.0.7.1");var subQ1=sQuery(id+"F1.wireOp",EDGE,"E3.1.0.0");var subQ2=makeQuery(id+"F1.imprint","INTERSECT",VERTEX,{"derivedFrom":[subQ1,subQ0]});Q145=makeQuery(id+"F1.imprint","IMPRINT",FACE,{"disambiguationData":[TD([[makeQuery(id+"F1.imprint","IMPRINT",EDGE,{"disambiguationData":[TD([[subQ2,-1.0]])],"derivedFrom":subQ1}),1.0]])]});}
            var Q146;
            {var subQ0=sQuery(id+"F1.wireOp",EDGE,"E5.0.4.1");var subQ1=sQuery(id+"F1.wireOp",EDGE,"E2.left");var subQ2=makeQuery(id+"F1.imprint","INTERSECT",VERTEX,{"derivedFrom":[subQ1,subQ0]});Q146=makeQuery(id+"F1.imprint","IMPRINT",FACE,{"disambiguationData":[TD([[makeQuery(id+"F1.imprint","IMPRINT",EDGE,{"disambiguationData":[TD([[subQ2,-1.0]])],"derivedFrom":subQ1}),1.0]])]});}
            var Q147;
            {var subQ0=sQuery(id+"F1.wireOp",EDGE,"E5.0.2.0");var subQ1=sQuery(id+"F1.wireOp",EDGE,"E3.8.0.0");var subQ2=makeQuery(id+"F1.imprint","INTERSECT",VERTEX,{"derivedFrom":[subQ1,subQ0]});Q147=makeQuery(id+"F1.imprint","IMPRINT",FACE,{"disambiguationData":[TD([[makeQuery(id+"F1.imprint","IMPRINT",EDGE,{"disambiguationData":[TD([[subQ2,1.0]])],"derivedFrom":subQ1}),1.0]])]});}
            var Q148;
            {var subQ0=sQuery(id+"F1.wireOp",EDGE,"E5.0.7.1");var subQ1=sQuery(id+"F1.wireOp",EDGE,"E3.2.0.0");var subQ2=makeQuery(id+"F1.imprint","INTERSECT",VERTEX,{"derivedFrom":[subQ1,subQ0]});Q148=makeQuery(id+"F1.imprint","IMPRINT",FACE,{"disambiguationData":[TD([[makeQuery(id+"F1.imprint","IMPRINT",EDGE,{"disambiguationData":[TD([[subQ2,-1.0]])],"derivedFrom":subQ1}),1.0]])]});}
            var Q149;
            {var subQ0=sQuery(id+"F1.wireOp",EDGE,"E5.0.5.0");var subQ1=sQuery(id+"F1.wireOp",EDGE,"E3.4.0.1");var subQ2=makeQuery(id+"F1.imprint","INTERSECT",VERTEX,{"derivedFrom":[subQ1,subQ0]});Q149=makeQuery(id+"F1.imprint","IMPRINT",FACE,{"disambiguationData":[TD([[makeQuery(id+"F1.imprint","IMPRINT",EDGE,{"disambiguationData":[TD([[subQ2,-1.0]])],"derivedFrom":subQ1}),1.0]])]});}
            var Q150;
            {var subQ0=sQuery(id+"F1.wireOp",EDGE,"E5.0.3.0");var subQ1=sQuery(id+"F1.wireOp",EDGE,"E2.right");var subQ2=makeQuery(id+"F1.imprint","INTERSECT",VERTEX,{"derivedFrom":[subQ1,subQ0]});Q150=makeQuery(id+"F1.imprint","IMPRINT",FACE,{"disambiguationData":[TD([[makeQuery(id+"F1.imprint","IMPRINT",EDGE,{"disambiguationData":[TD([[subQ2,-1.0]])],"derivedFrom":subQ1}),1.0]])]});}
            var Q151;
            {var subQ0=sQuery(id+"F1.wireOp",EDGE,"E5.0.7.0");var subQ1=sQuery(id+"F1.wireOp",EDGE,"E3.8.0.0");var subQ2=makeQuery(id+"F1.imprint","INTERSECT",VERTEX,{"derivedFrom":[subQ1,subQ0]});Q151=makeQuery(id+"F1.imprint","IMPRINT",FACE,{"disambiguationData":[TD([[makeQuery(id+"F1.imprint","IMPRINT",EDGE,{"disambiguationData":[TD([[subQ2,-1.0]])],"derivedFrom":subQ1}),1.0]])]});}
            var Q152;
            {var subQ0=sQuery(id+"F1.wireOp",EDGE,"E5.0.3.1");var subQ1=sQuery(id+"F1.wireOp",EDGE,"E3.4.0.1");var subQ2=makeQuery(id+"F1.imprint","INTERSECT",VERTEX,{"derivedFrom":[subQ1,subQ0]});Q152=makeQuery(id+"F1.imprint","IMPRINT",FACE,{"disambiguationData":[TD([[makeQuery(id+"F1.imprint","IMPRINT",EDGE,{"disambiguationData":[TD([[subQ2,1.0]])],"derivedFrom":subQ1}),1.0]])]});}
            var Q153;
            {var subQ0=sQuery(id+"F1.wireOp",EDGE,"E5.0.2.1");var subQ1=sQuery(id+"F1.wireOp",EDGE,"E3.1.0.0");var subQ2=makeQuery(id+"F1.imprint","INTERSECT",VERTEX,{"derivedFrom":[subQ1,subQ0]});Q153=makeQuery(id+"F1.imprint","IMPRINT",FACE,{"disambiguationData":[TD([[makeQuery(id+"F1.imprint","IMPRINT",EDGE,{"disambiguationData":[TD([[subQ2,-1.0]])],"derivedFrom":subQ1}),1.0]])]});}
            var Q154;
            {var subQ0=sQuery(id+"F1.wireOp",EDGE,"E5.0.4.1");var subQ1=sQuery(id+"F1.wireOp",EDGE,"E3.5.0.1");var subQ2=makeQuery(id+"F1.imprint","INTERSECT",VERTEX,{"derivedFrom":[subQ1,subQ0]});Q154=makeQuery(id+"F1.imprint","IMPRINT",FACE,{"disambiguationData":[TD([[makeQuery(id+"F1.imprint","IMPRINT",EDGE,{"disambiguationData":[TD([[subQ2,1.0]])],"derivedFrom":subQ1}),1.0]])]});}
            var Q155;
            {var subQ0=sQuery(id+"F1.wireOp",EDGE,"E5.0.3.1");var subQ1=sQuery(id+"F1.wireOp",EDGE,"E3.7.0.0");var subQ2=makeQuery(id+"F1.imprint","INTERSECT",VERTEX,{"derivedFrom":[subQ1,subQ0]});Q155=makeQuery(id+"F1.imprint","IMPRINT",FACE,{"disambiguationData":[TD([[makeQuery(id+"F1.imprint","IMPRINT",EDGE,{"disambiguationData":[TD([[subQ2,1.0]])],"derivedFrom":subQ1}),1.0]])]});}
            var Q156;
            {var subQ0=sQuery(id+"F1.wireOp",EDGE,"E4.top");var subQ1=sQuery(id+"F1.wireOp",EDGE,"E3.4.0.0");var subQ2=makeQuery(id+"F1.imprint","INTERSECT",VERTEX,{"derivedFrom":[subQ1,subQ0]});Q156=makeQuery(id+"F1.imprint","IMPRINT",FACE,{"disambiguationData":[TD([[makeQuery(id+"F1.imprint","IMPRINT",EDGE,{"disambiguationData":[TD([[subQ2,1.0]])],"derivedFrom":subQ1}),1.0]])]});}
            var Q157;
            {var subQ0=sQuery(id+"F1.wireOp",EDGE,"E5.0.5.1");var subQ1=sQuery(id+"F1.wireOp",EDGE,"E3.7.0.1");var subQ2=makeQuery(id+"F1.imprint","INTERSECT",VERTEX,{"derivedFrom":[subQ1,subQ0]});Q157=makeQuery(id+"F1.imprint","IMPRINT",FACE,{"disambiguationData":[TD([[makeQuery(id+"F1.imprint","IMPRINT",EDGE,{"disambiguationData":[TD([[subQ2,1.0]])],"derivedFrom":subQ1}),1.0]])]});}
            var Q158;
            {var subQ0=sQuery(id+"F1.wireOp",EDGE,"E5.0.7.0");var subQ1=sQuery(id+"F1.wireOp",EDGE,"E3.5.0.1");var subQ2=makeQuery(id+"F1.imprint","INTERSECT",VERTEX,{"derivedFrom":[subQ1,subQ0]});Q158=makeQuery(id+"F1.imprint","IMPRINT",FACE,{"disambiguationData":[TD([[makeQuery(id+"F1.imprint","IMPRINT",EDGE,{"disambiguationData":[TD([[subQ2,-1.0]])],"derivedFrom":subQ1}),1.0]])]});}
            var Q159;
            {var subQ0=sQuery(id+"F1.wireOp",EDGE,"E5.0.3.1");var subQ1=sQuery(id+"F1.wireOp",EDGE,"E3.1.0.0");var subQ2=makeQuery(id+"F1.imprint","INTERSECT",VERTEX,{"derivedFrom":[subQ1,subQ0]});Q159=makeQuery(id+"F1.imprint","IMPRINT",FACE,{"disambiguationData":[TD([[makeQuery(id+"F1.imprint","IMPRINT",EDGE,{"disambiguationData":[TD([[subQ2,1.0]])],"derivedFrom":subQ1}),1.0]])]});}
            var Q160;
            {var subQ0=sQuery(id+"F1.wireOp",EDGE,"E5.0.8.1");var subQ1=sQuery(id+"F1.wireOp",EDGE,"E3.6.0.0");var subQ2=makeQuery(id+"F1.imprint","INTERSECT",VERTEX,{"derivedFrom":[subQ1,subQ0]});Q160=makeQuery(id+"F1.imprint","IMPRINT",FACE,{"disambiguationData":[TD([[makeQuery(id+"F1.imprint","IMPRINT",EDGE,{"disambiguationData":[TD([[subQ2,1.0]])],"derivedFrom":subQ1}),1.0]])]});}
            var Q161;
            {var subQ0=sQuery(id+"F1.wireOp",EDGE,"E5.0.7.1");var subQ1=sQuery(id+"F1.wireOp",EDGE,"E3.3.0.0");var subQ2=makeQuery(id+"F1.imprint","INTERSECT",VERTEX,{"derivedFrom":[subQ1,subQ0]});Q161=makeQuery(id+"F1.imprint","IMPRINT",FACE,{"disambiguationData":[TD([[makeQuery(id+"F1.imprint","IMPRINT",EDGE,{"disambiguationData":[TD([[subQ2,-1.0]])],"derivedFrom":subQ1}),1.0]])]});}
            var Q162;
            {var subQ0=sQuery(id+"F1.wireOp",EDGE,"E5.0.5.0");var subQ1=sQuery(id+"F1.wireOp",EDGE,"E3.4.0.0");var subQ2=makeQuery(id+"F1.imprint","INTERSECT",VERTEX,{"derivedFrom":[subQ1,subQ0]});Q162=makeQuery(id+"F1.imprint","IMPRINT",FACE,{"disambiguationData":[TD([[makeQuery(id+"F1.imprint","IMPRINT",EDGE,{"disambiguationData":[TD([[subQ2,-1.0]])],"derivedFrom":subQ1}),1.0]])]});}
            var Q163;
            {var subQ0=sQuery(id+"F1.wireOp",EDGE,"E5.0.3.0");var subQ1=sQuery(id+"F1.wireOp",EDGE,"E3.6.0.0");var subQ2=makeQuery(id+"F1.imprint","INTERSECT",VERTEX,{"derivedFrom":[subQ1,subQ0]});Q163=makeQuery(id+"F1.imprint","IMPRINT",FACE,{"disambiguationData":[TD([[makeQuery(id+"F1.imprint","IMPRINT",EDGE,{"disambiguationData":[TD([[subQ2,1.0]])],"derivedFrom":subQ1}),1.0]])]});}
            var Q164;
            {var subQ0=sQuery(id+"F1.wireOp",EDGE,"E5.0.7.0");var subQ1=sQuery(id+"F1.wireOp",EDGE,"E3.2.0.0");var subQ2=makeQuery(id+"F1.imprint","INTERSECT",VERTEX,{"derivedFrom":[subQ1,subQ0]});Q164=makeQuery(id+"F1.imprint","IMPRINT",FACE,{"disambiguationData":[TD([[makeQuery(id+"F1.imprint","IMPRINT",EDGE,{"disambiguationData":[TD([[subQ2,-1.0]])],"derivedFrom":subQ1}),1.0]])]});}
            var Q165;
            {var subQ0=sQuery(id+"F1.wireOp",EDGE,"E5.0.5.1");var subQ1=sQuery(id+"F1.wireOp",EDGE,"E2.left");var subQ2=makeQuery(id+"F1.imprint","INTERSECT",VERTEX,{"derivedFrom":[subQ1,subQ0]});Q165=makeQuery(id+"F1.imprint","IMPRINT",FACE,{"disambiguationData":[TD([[makeQuery(id+"F1.imprint","IMPRINT",EDGE,{"disambiguationData":[TD([[subQ2,-1.0]])],"derivedFrom":subQ1}),1.0]])]});}
            var Q166;
            {var subQ0=sQuery(id+"F1.wireOp",EDGE,"E5.0.6.0");var subQ1=sQuery(id+"F1.wireOp",EDGE,"E2.right");var subQ2=makeQuery(id+"F1.imprint","INTERSECT",VERTEX,{"derivedFrom":[subQ1,subQ0]});Q166=makeQuery(id+"F1.imprint","IMPRINT",FACE,{"disambiguationData":[TD([[makeQuery(id+"F1.imprint","IMPRINT",EDGE,{"disambiguationData":[TD([[subQ2,-1.0]])],"derivedFrom":subQ1}),1.0]])]});}
            var Q167;
            {var subQ0=sQuery(id+"F1.wireOp",EDGE,"E4.bottom");var subQ1=sQuery(id+"F1.wireOp",EDGE,"E3.3.0.1");var subQ2=makeQuery(id+"F1.imprint","INTERSECT",VERTEX,{"derivedFrom":[subQ1,subQ0]});Q167=makeQuery(id+"F1.imprint","IMPRINT",FACE,{"disambiguationData":[TD([[makeQuery(id+"F1.imprint","IMPRINT",EDGE,{"disambiguationData":[TD([[subQ2,-1.0]])],"derivedFrom":subQ1}),1.0]])]});}
            var Q168;
            {var subQ0=sQuery(id+"F1.wireOp",EDGE,"E5.0.5.0");var subQ1=sQuery(id+"F1.wireOp",EDGE,"E3.3.0.0");var subQ2=makeQuery(id+"F1.imprint","INTERSECT",VERTEX,{"derivedFrom":[subQ1,subQ0]});Q168=makeQuery(id+"F1.imprint","IMPRINT",FACE,{"disambiguationData":[TD([[makeQuery(id+"F1.imprint","IMPRINT",EDGE,{"disambiguationData":[TD([[subQ2,-1.0]])],"derivedFrom":subQ1}),1.0]])]});}
            var Q169;
            {var subQ0=sQuery(id+"F1.wireOp",EDGE,"E5.0.4.1");var subQ1=sQuery(id+"F1.wireOp",EDGE,"E3.7.0.1");var subQ2=makeQuery(id+"F1.imprint","INTERSECT",VERTEX,{"derivedFrom":[subQ1,subQ0]});Q169=makeQuery(id+"F1.imprint","IMPRINT",FACE,{"disambiguationData":[TD([[makeQuery(id+"F1.imprint","IMPRINT",EDGE,{"disambiguationData":[TD([[subQ2,1.0]])],"derivedFrom":subQ1}),1.0]])]});}
            var Q170;
            {var subQ0=sQuery(id+"F1.wireOp",EDGE,"E4.top");var subQ1=sQuery(id+"F1.wireOp",EDGE,"E3.5.0.0");var subQ2=makeQuery(id+"F1.imprint","INTERSECT",VERTEX,{"derivedFrom":[subQ1,subQ0]});Q170=makeQuery(id+"F1.imprint","IMPRINT",FACE,{"disambiguationData":[TD([[makeQuery(id+"F1.imprint","IMPRINT",EDGE,{"disambiguationData":[TD([[subQ2,-1.0]])],"derivedFrom":subQ1}),1.0]])]});}
            var Q171;
            {var subQ0=sQuery(id+"F1.wireOp",EDGE,"E5.0.6.1");var subQ1=sQuery(id+"F1.wireOp",EDGE,"E3.3.0.0");var subQ2=makeQuery(id+"F1.imprint","INTERSECT",VERTEX,{"derivedFrom":[subQ1,subQ0]});Q171=makeQuery(id+"F1.imprint","IMPRINT",FACE,{"disambiguationData":[TD([[makeQuery(id+"F1.imprint","IMPRINT",EDGE,{"disambiguationData":[TD([[subQ2,-1.0]])],"derivedFrom":subQ1}),1.0]])]});}
            var Q172;
            {var subQ0=sQuery(id+"F1.wireOp",EDGE,"E5.0.8.0");var subQ1=sQuery(id+"F1.wireOp",EDGE,"E3.3.0.1");var subQ2=makeQuery(id+"F1.imprint","INTERSECT",VERTEX,{"derivedFrom":[subQ1,subQ0]});Q172=makeQuery(id+"F1.imprint","IMPRINT",FACE,{"disambiguationData":[TD([[makeQuery(id+"F1.imprint","IMPRINT",EDGE,{"disambiguationData":[TD([[subQ2,-1.0]])],"derivedFrom":subQ1}),1.0]])]});}
            var Q173;
            {var subQ0=sQuery(id+"F1.wireOp",EDGE,"E5.0.4.1");var subQ1=sQuery(id+"F1.wireOp",EDGE,"E2.left");var subQ2=makeQuery(id+"F1.imprint","INTERSECT",VERTEX,{"derivedFrom":[subQ1,subQ0]});Q173=makeQuery(id+"F1.imprint","IMPRINT",FACE,{"disambiguationData":[TD([[makeQuery(id+"F1.imprint","IMPRINT",EDGE,{"disambiguationData":[TD([[subQ2,1.0]])],"derivedFrom":subQ1}),1.0]])]});}
            var Q174;
            {var subQ0=sQuery(id+"F1.wireOp",EDGE,"E5.0.1.0");var subQ1=sQuery(id+"F1.wireOp",EDGE,"E3.8.0.0");var subQ2=makeQuery(id+"F1.imprint","INTERSECT",VERTEX,{"derivedFrom":[subQ1,subQ0]});Q174=makeQuery(id+"F1.imprint","IMPRINT",FACE,{"disambiguationData":[TD([[makeQuery(id+"F1.imprint","IMPRINT",EDGE,{"disambiguationData":[TD([[subQ2,-1.0]])],"derivedFrom":subQ1}),1.0]])]});}
            var Q175;
            {var subQ0=sQuery(id+"F1.wireOp",EDGE,"E5.0.3.1");var subQ1=sQuery(id+"F1.wireOp",EDGE,"E3.8.0.0");var subQ2=makeQuery(id+"F1.imprint","INTERSECT",VERTEX,{"derivedFrom":[subQ1,subQ0]});Q175=makeQuery(id+"F1.imprint","IMPRINT",FACE,{"disambiguationData":[TD([[makeQuery(id+"F1.imprint","IMPRINT",EDGE,{"disambiguationData":[TD([[subQ2,-1.0]])],"derivedFrom":subQ1}),1.0]])]});}
            var Q176;
            {var subQ0=sQuery(id+"F1.wireOp",EDGE,"E5.0.1.0");var subQ1=sQuery(id+"F1.wireOp",EDGE,"E3.8.0.0");var subQ2=makeQuery(id+"F1.imprint","INTERSECT",VERTEX,{"derivedFrom":[subQ1,subQ0]});Q176=makeQuery(id+"F1.imprint","IMPRINT",FACE,{"disambiguationData":[TD([[makeQuery(id+"F1.imprint","IMPRINT",EDGE,{"disambiguationData":[TD([[subQ2,1.0]])],"derivedFrom":subQ1}),1.0]])]});}
            var Q177;
            {var subQ0=sQuery(id+"F1.wireOp",EDGE,"E5.0.4.0");var subQ1=sQuery(id+"F1.wireOp",EDGE,"E3.1.0.0");var subQ2=makeQuery(id+"F1.imprint","INTERSECT",VERTEX,{"derivedFrom":[subQ1,subQ0]});Q177=makeQuery(id+"F1.imprint","IMPRINT",FACE,{"disambiguationData":[TD([[makeQuery(id+"F1.imprint","IMPRINT",EDGE,{"disambiguationData":[TD([[subQ2,-1.0]])],"derivedFrom":subQ1}),1.0]])]});}
            var Q178;
            {var subQ0=sQuery(id+"F1.wireOp",EDGE,"E4.top");var subQ1=sQuery(id+"F1.wireOp",EDGE,"E3.5.0.1");var subQ2=makeQuery(id+"F1.imprint","INTERSECT",VERTEX,{"derivedFrom":[subQ1,subQ0]});Q178=makeQuery(id+"F1.imprint","IMPRINT",FACE,{"disambiguationData":[TD([[makeQuery(id+"F1.imprint","IMPRINT",EDGE,{"disambiguationData":[TD([[subQ2,1.0]])],"derivedFrom":subQ1}),1.0]])]});}
            var Q179;
            {var subQ0=sQuery(id+"F1.wireOp",EDGE,"E5.0.5.0");var subQ1=sQuery(id+"F1.wireOp",EDGE,"E3.2.0.1");var subQ2=makeQuery(id+"F1.imprint","INTERSECT",VERTEX,{"derivedFrom":[subQ1,subQ0]});Q179=makeQuery(id+"F1.imprint","IMPRINT",FACE,{"disambiguationData":[TD([[makeQuery(id+"F1.imprint","IMPRINT",EDGE,{"disambiguationData":[TD([[subQ2,-1.0]])],"derivedFrom":subQ1}),1.0]])]});}
            var Q180;
            {var subQ0=sQuery(id+"F1.wireOp",EDGE,"E5.0.2.1");var subQ1=sQuery(id+"F1.wireOp",EDGE,"E3.3.0.1");var subQ2=makeQuery(id+"F1.imprint","INTERSECT",VERTEX,{"derivedFrom":[subQ1,subQ0]});Q180=makeQuery(id+"F1.imprint","IMPRINT",FACE,{"disambiguationData":[TD([[makeQuery(id+"F1.imprint","IMPRINT",EDGE,{"disambiguationData":[TD([[subQ2,1.0]])],"derivedFrom":subQ1}),1.0]])]});}
            var Q181;
            {var subQ0=sQuery(id+"F1.wireOp",EDGE,"E5.0.8.1");var subQ1=sQuery(id+"F1.wireOp",EDGE,"E3.4.0.0");var subQ2=makeQuery(id+"F1.imprint","INTERSECT",VERTEX,{"derivedFrom":[subQ1,subQ0]});Q181=makeQuery(id+"F1.imprint","IMPRINT",FACE,{"disambiguationData":[TD([[makeQuery(id+"F1.imprint","IMPRINT",EDGE,{"disambiguationData":[TD([[subQ2,1.0]])],"derivedFrom":subQ1}),1.0]])]});}
            var Q182;
            {var subQ0=sQuery(id+"F1.wireOp",EDGE,"E5.0.3.0");var subQ1=sQuery(id+"F1.wireOp",EDGE,"E3.3.0.1");var subQ2=makeQuery(id+"F1.imprint","INTERSECT",VERTEX,{"derivedFrom":[subQ1,subQ0]});Q182=makeQuery(id+"F1.imprint","IMPRINT",FACE,{"disambiguationData":[TD([[makeQuery(id+"F1.imprint","IMPRINT",EDGE,{"disambiguationData":[TD([[subQ2,-1.0]])],"derivedFrom":subQ1}),1.0]])]});}
            var Q183;
            {var subQ0=sQuery(id+"F1.wireOp",EDGE,"E5.0.2.1");var subQ1=sQuery(id+"F1.wireOp",EDGE,"E3.5.0.0");var subQ2=makeQuery(id+"F1.imprint","INTERSECT",VERTEX,{"derivedFrom":[subQ1,subQ0]});Q183=makeQuery(id+"F1.imprint","IMPRINT",FACE,{"disambiguationData":[TD([[makeQuery(id+"F1.imprint","IMPRINT",EDGE,{"disambiguationData":[TD([[subQ2,1.0]])],"derivedFrom":subQ1}),1.0]])]});}
            var Q184;
            {var subQ0=sQuery(id+"F1.wireOp",EDGE,"E5.0.3.0");var subQ1=sQuery(id+"F1.wireOp",EDGE,"E3.2.0.0");var subQ2=makeQuery(id+"F1.imprint","INTERSECT",VERTEX,{"derivedFrom":[subQ1,subQ0]});Q184=makeQuery(id+"F1.imprint","IMPRINT",FACE,{"disambiguationData":[TD([[makeQuery(id+"F1.imprint","IMPRINT",EDGE,{"disambiguationData":[TD([[subQ2,1.0]])],"derivedFrom":subQ1}),1.0]])]});}
            var Q185;
            {var subQ0=sQuery(id+"F1.wireOp",EDGE,"E5.0.4.1");var subQ1=sQuery(id+"F1.wireOp",EDGE,"E3.6.0.0");var subQ2=makeQuery(id+"F1.imprint","INTERSECT",VERTEX,{"derivedFrom":[subQ1,subQ0]});Q185=makeQuery(id+"F1.imprint","IMPRINT",FACE,{"disambiguationData":[TD([[makeQuery(id+"F1.imprint","IMPRINT",EDGE,{"disambiguationData":[TD([[subQ2,-1.0]])],"derivedFrom":subQ1}),1.0]])]});}
            var Q186;
            {var subQ0=sQuery(id+"F1.wireOp",EDGE,"E5.0.6.1");var subQ1=sQuery(id+"F1.wireOp",EDGE,"E3.2.0.1");var subQ2=makeQuery(id+"F1.imprint","INTERSECT",VERTEX,{"derivedFrom":[subQ1,subQ0]});Q186=makeQuery(id+"F1.imprint","IMPRINT",FACE,{"disambiguationData":[TD([[makeQuery(id+"F1.imprint","IMPRINT",EDGE,{"disambiguationData":[TD([[subQ2,1.0]])],"derivedFrom":subQ1}),1.0]])]});}
            var Q187;
            {var subQ0=sQuery(id+"F1.wireOp",EDGE,"E5.0.6.1");var subQ1=sQuery(id+"F1.wireOp",EDGE,"E3.7.0.1");var subQ2=makeQuery(id+"F1.imprint","INTERSECT",VERTEX,{"derivedFrom":[subQ1,subQ0]});Q187=makeQuery(id+"F1.imprint","IMPRINT",FACE,{"disambiguationData":[TD([[makeQuery(id+"F1.imprint","IMPRINT",EDGE,{"disambiguationData":[TD([[subQ2,1.0]])],"derivedFrom":subQ1}),1.0]])]});}
            var Q188;
            {var subQ0=sQuery(id+"F1.wireOp",EDGE,"E5.0.7.0");var subQ1=sQuery(id+"F1.wireOp",EDGE,"E2.right");var subQ2=makeQuery(id+"F1.imprint","INTERSECT",VERTEX,{"derivedFrom":[subQ1,subQ0]});Q188=makeQuery(id+"F1.imprint","IMPRINT",FACE,{"disambiguationData":[TD([[makeQuery(id+"F1.imprint","IMPRINT",EDGE,{"disambiguationData":[TD([[subQ2,-1.0]])],"derivedFrom":subQ1}),1.0]])]});}
            var Q189;
            {var subQ0=sQuery(id+"F1.wireOp",EDGE,"E5.0.3.1");var subQ1=sQuery(id+"F1.wireOp",EDGE,"E3.6.0.0");var subQ2=makeQuery(id+"F1.imprint","INTERSECT",VERTEX,{"derivedFrom":[subQ1,subQ0]});Q189=makeQuery(id+"F1.imprint","IMPRINT",FACE,{"disambiguationData":[TD([[makeQuery(id+"F1.imprint","IMPRINT",EDGE,{"disambiguationData":[TD([[subQ2,-1.0]])],"derivedFrom":subQ1}),1.0]])]});}
            var Q190;
            {var subQ0=sQuery(id+"F1.wireOp",EDGE,"E5.0.6.0");var subQ1=sQuery(id+"F1.wireOp",EDGE,"E3.3.0.0");var subQ2=makeQuery(id+"F1.imprint","INTERSECT",VERTEX,{"derivedFrom":[subQ1,subQ0]});Q190=makeQuery(id+"F1.imprint","IMPRINT",FACE,{"disambiguationData":[TD([[makeQuery(id+"F1.imprint","IMPRINT",EDGE,{"disambiguationData":[TD([[subQ2,1.0]])],"derivedFrom":subQ1}),1.0]])]});}
            var Q191;
            {var subQ0=sQuery(id+"F1.wireOp",EDGE,"E5.0.4.1");var subQ1=sQuery(id+"F1.wireOp",EDGE,"E3.8.0.0");var subQ2=makeQuery(id+"F1.imprint","INTERSECT",VERTEX,{"derivedFrom":[subQ1,subQ0]});Q191=makeQuery(id+"F1.imprint","IMPRINT",FACE,{"disambiguationData":[TD([[makeQuery(id+"F1.imprint","IMPRINT",EDGE,{"disambiguationData":[TD([[subQ2,1.0]])],"derivedFrom":subQ1}),1.0]])]});}
            var Q192;
            {var subQ0=sQuery(id+"F1.wireOp",EDGE,"E5.0.1.1");var subQ1=sQuery(id+"F1.wireOp",EDGE,"E3.4.0.1");var subQ2=makeQuery(id+"F1.imprint","INTERSECT",VERTEX,{"derivedFrom":[subQ1,subQ0]});Q192=makeQuery(id+"F1.imprint","IMPRINT",FACE,{"disambiguationData":[TD([[makeQuery(id+"F1.imprint","IMPRINT",EDGE,{"disambiguationData":[TD([[subQ2,1.0]])],"derivedFrom":subQ1}),1.0]])]});}
            var Q193;
            {var subQ0=sQuery(id+"F1.wireOp",EDGE,"E5.0.5.0");var subQ1=sQuery(id+"F1.wireOp",EDGE,"E3.5.0.1");var subQ2=makeQuery(id+"F1.imprint","INTERSECT",VERTEX,{"derivedFrom":[subQ1,subQ0]});Q193=makeQuery(id+"F1.imprint","IMPRINT",FACE,{"disambiguationData":[TD([[makeQuery(id+"F1.imprint","IMPRINT",EDGE,{"disambiguationData":[TD([[subQ2,-1.0]])],"derivedFrom":subQ1}),1.0]])]});}
            var Q194;
            {var subQ0=sQuery(id+"F1.wireOp",EDGE,"E5.0.7.0");var subQ1=sQuery(id+"F1.wireOp",EDGE,"E3.8.0.0");var subQ2=makeQuery(id+"F1.imprint","INTERSECT",VERTEX,{"derivedFrom":[subQ1,subQ0]});Q194=makeQuery(id+"F1.imprint","IMPRINT",FACE,{"disambiguationData":[TD([[makeQuery(id+"F1.imprint","IMPRINT",EDGE,{"disambiguationData":[TD([[subQ2,1.0]])],"derivedFrom":subQ1}),1.0]])]});}
            var Q195;
            {var subQ0=sQuery(id+"F1.wireOp",EDGE,"E4.top");var subQ1=sQuery(id+"F1.wireOp",EDGE,"E3.6.0.0");var subQ2=makeQuery(id+"F1.imprint","INTERSECT",VERTEX,{"derivedFrom":[subQ1,subQ0]});Q195=makeQuery(id+"F1.imprint","IMPRINT",FACE,{"disambiguationData":[TD([[makeQuery(id+"F1.imprint","IMPRINT",EDGE,{"disambiguationData":[TD([[subQ2,-1.0]])],"derivedFrom":subQ1}),1.0]])]});}
            var Q196;
            {var subQ0=sQuery(id+"F1.wireOp",EDGE,"E5.0.6.1");var subQ1=sQuery(id+"F1.wireOp",EDGE,"E3.4.0.0");var subQ2=makeQuery(id+"F1.imprint","INTERSECT",VERTEX,{"derivedFrom":[subQ1,subQ0]});Q196=makeQuery(id+"F1.imprint","IMPRINT",FACE,{"disambiguationData":[TD([[makeQuery(id+"F1.imprint","IMPRINT",EDGE,{"disambiguationData":[TD([[subQ2,-1.0]])],"derivedFrom":subQ1}),1.0]])]});}
            var Q197;
            {var subQ0=sQuery(id+"F1.wireOp",EDGE,"E5.0.7.0");var subQ1=sQuery(id+"F1.wireOp",EDGE,"E3.4.0.1");var subQ2=makeQuery(id+"F1.imprint","INTERSECT",VERTEX,{"derivedFrom":[subQ1,subQ0]});Q197=makeQuery(id+"F1.imprint","IMPRINT",FACE,{"disambiguationData":[TD([[makeQuery(id+"F1.imprint","IMPRINT",EDGE,{"disambiguationData":[TD([[subQ2,-1.0]])],"derivedFrom":subQ1}),1.0]])]});}
            var Q198;
            {var subQ0=sQuery(id+"F1.wireOp",EDGE,"E5.0.1.0");var subQ1=sQuery(id+"F1.wireOp",EDGE,"E2.left");var subQ2=makeQuery(id+"F1.imprint","INTERSECT",VERTEX,{"derivedFrom":[subQ1,subQ0]});Q198=makeQuery(id+"F1.imprint","IMPRINT",FACE,{"disambiguationData":[TD([[makeQuery(id+"F1.imprint","IMPRINT",EDGE,{"disambiguationData":[TD([[subQ2,1.0]])],"derivedFrom":subQ1}),1.0]])]});}
            var Q199;
            {var subQ0=sQuery(id+"F1.wireOp",EDGE,"E5.0.6.1");var subQ1=sQuery(id+"F1.wireOp",EDGE,"E3.6.0.0");var subQ2=makeQuery(id+"F1.imprint","INTERSECT",VERTEX,{"derivedFrom":[subQ1,subQ0]});Q199=makeQuery(id+"F1.imprint","IMPRINT",FACE,{"disambiguationData":[TD([[makeQuery(id+"F1.imprint","IMPRINT",EDGE,{"disambiguationData":[TD([[subQ2,1.0]])],"derivedFrom":subQ1}),1.0]])]});}
            var Q200;
            {var subQ0=sQuery(id+"F1.wireOp",EDGE,"E5.0.6.1");var subQ1=sQuery(id+"F1.wireOp",EDGE,"E3.8.0.0");var subQ2=makeQuery(id+"F1.imprint","INTERSECT",VERTEX,{"derivedFrom":[subQ1,subQ0]});Q200=makeQuery(id+"F1.imprint","IMPRINT",FACE,{"disambiguationData":[TD([[makeQuery(id+"F1.imprint","IMPRINT",EDGE,{"disambiguationData":[TD([[subQ2,1.0]])],"derivedFrom":subQ1}),1.0]])]});}
            var Q201;
            {var subQ0=sQuery(id+"F1.wireOp",EDGE,"E5.0.6.0");var subQ1=sQuery(id+"F1.wireOp",EDGE,"E3.4.0.0");var subQ2=makeQuery(id+"F1.imprint","INTERSECT",VERTEX,{"derivedFrom":[subQ1,subQ0]});Q201=makeQuery(id+"F1.imprint","IMPRINT",FACE,{"disambiguationData":[TD([[makeQuery(id+"F1.imprint","IMPRINT",EDGE,{"disambiguationData":[TD([[subQ2,1.0]])],"derivedFrom":subQ1}),1.0]])]});}
            var Q202;
            {var subQ0=sQuery(id+"F1.wireOp",EDGE,"E5.0.8.1");var subQ1=sQuery(id+"F1.wireOp",EDGE,"E3.7.0.1");var subQ2=makeQuery(id+"F1.imprint","INTERSECT",VERTEX,{"derivedFrom":[subQ1,subQ0]});Q202=makeQuery(id+"F1.imprint","IMPRINT",FACE,{"disambiguationData":[TD([[makeQuery(id+"F1.imprint","IMPRINT",EDGE,{"disambiguationData":[TD([[subQ2,1.0]])],"derivedFrom":subQ1}),1.0]])]});}
            var Q203;
            {var subQ0=sQuery(id+"F1.wireOp",EDGE,"E5.0.5.0");var subQ1=sQuery(id+"F1.wireOp",EDGE,"E2.right");var subQ2=makeQuery(id+"F1.imprint","INTERSECT",VERTEX,{"derivedFrom":[subQ1,subQ0]});Q203=makeQuery(id+"F1.imprint","IMPRINT",FACE,{"disambiguationData":[TD([[makeQuery(id+"F1.imprint","IMPRINT",EDGE,{"disambiguationData":[TD([[subQ2,-1.0]])],"derivedFrom":subQ1}),1.0]])]});}
            var Q204;
            {var subQ0=sQuery(id+"F1.wireOp",EDGE,"E4.top");var subQ1=sQuery(id+"F1.wireOp",EDGE,"E3.1.0.0");var subQ2=makeQuery(id+"F1.imprint","INTERSECT",VERTEX,{"derivedFrom":[subQ1,subQ0]});Q204=makeQuery(id+"F1.imprint","IMPRINT",FACE,{"disambiguationData":[TD([[makeQuery(id+"F1.imprint","IMPRINT",EDGE,{"disambiguationData":[TD([[subQ2,-1.0]])],"derivedFrom":subQ1}),1.0]])]});}
            var Q205;
            {var subQ0=sQuery(id+"F1.wireOp",EDGE,"E4.top");var subQ1=sQuery(id+"F1.wireOp",EDGE,"E3.2.0.0");var subQ2=makeQuery(id+"F1.imprint","INTERSECT",VERTEX,{"derivedFrom":[subQ1,subQ0]});Q205=makeQuery(id+"F1.imprint","IMPRINT",FACE,{"disambiguationData":[TD([[makeQuery(id+"F1.imprint","IMPRINT",EDGE,{"disambiguationData":[TD([[subQ2,1.0]])],"derivedFrom":subQ1}),1.0]])]});}
            var Q206;
            {var subQ0=sQuery(id+"F1.wireOp",EDGE,"E5.0.6.1");var subQ1=sQuery(id+"F1.wireOp",EDGE,"E3.4.0.0");var subQ2=makeQuery(id+"F1.imprint","INTERSECT",VERTEX,{"derivedFrom":[subQ1,subQ0]});Q206=makeQuery(id+"F1.imprint","IMPRINT",FACE,{"disambiguationData":[TD([[makeQuery(id+"F1.imprint","IMPRINT",EDGE,{"disambiguationData":[TD([[subQ2,1.0]])],"derivedFrom":subQ1}),1.0]])]});}
            var Q207;
            {var subQ0=sQuery(id+"F1.wireOp",EDGE,"E5.0.3.1");var subQ1=sQuery(id+"F1.wireOp",EDGE,"E3.7.0.0");var subQ2=makeQuery(id+"F1.imprint","INTERSECT",VERTEX,{"derivedFrom":[subQ1,subQ0]});Q207=makeQuery(id+"F1.imprint","IMPRINT",FACE,{"disambiguationData":[TD([[makeQuery(id+"F1.imprint","IMPRINT",EDGE,{"disambiguationData":[TD([[subQ2,-1.0]])],"derivedFrom":subQ1}),1.0]])]});}
            var Q208;
            {var subQ0=sQuery(id+"F1.wireOp",EDGE,"E5.0.1.1");var subQ1=sQuery(id+"F1.wireOp",EDGE,"E3.3.0.0");var subQ2=makeQuery(id+"F1.imprint","INTERSECT",VERTEX,{"derivedFrom":[subQ1,subQ0]});Q208=makeQuery(id+"F1.imprint","IMPRINT",FACE,{"disambiguationData":[TD([[makeQuery(id+"F1.imprint","IMPRINT",EDGE,{"disambiguationData":[TD([[subQ2,-1.0]])],"derivedFrom":subQ1}),1.0]])]});}
            var Q209;
            {var subQ0=sQuery(id+"F1.wireOp",EDGE,"E5.0.7.0");var subQ1=sQuery(id+"F1.wireOp",EDGE,"E3.7.0.0");var subQ2=makeQuery(id+"F1.imprint","INTERSECT",VERTEX,{"derivedFrom":[subQ1,subQ0]});Q209=makeQuery(id+"F1.imprint","IMPRINT",FACE,{"disambiguationData":[TD([[makeQuery(id+"F1.imprint","IMPRINT",EDGE,{"disambiguationData":[TD([[subQ2,-1.0]])],"derivedFrom":subQ1}),1.0]])]});}
            var Q210;
            {var subQ0=sQuery(id+"F1.wireOp",EDGE,"E5.0.6.1");var subQ1=sQuery(id+"F1.wireOp",EDGE,"E3.7.0.0");var subQ2=makeQuery(id+"F1.imprint","INTERSECT",VERTEX,{"derivedFrom":[subQ1,subQ0]});Q210=makeQuery(id+"F1.imprint","IMPRINT",FACE,{"disambiguationData":[TD([[makeQuery(id+"F1.imprint","IMPRINT",EDGE,{"disambiguationData":[TD([[subQ2,1.0]])],"derivedFrom":subQ1}),1.0]])]});}
            var Q211;
            {var subQ0=sQuery(id+"F1.wireOp",EDGE,"E4.bottom");var subQ1=sQuery(id+"F1.wireOp",EDGE,"E3.3.0.0");var subQ2=makeQuery(id+"F1.imprint","INTERSECT",VERTEX,{"derivedFrom":[subQ1,subQ0]});Q211=makeQuery(id+"F1.imprint","IMPRINT",FACE,{"disambiguationData":[TD([[makeQuery(id+"F1.imprint","IMPRINT",EDGE,{"disambiguationData":[TD([[subQ2,-1.0]])],"derivedFrom":subQ1}),1.0]])]});}
            var Q212;
            {var subQ0=sQuery(id+"F1.wireOp",EDGE,"E5.0.3.0");var subQ1=sQuery(id+"F1.wireOp",EDGE,"E3.3.0.0");var subQ2=makeQuery(id+"F1.imprint","INTERSECT",VERTEX,{"derivedFrom":[subQ1,subQ0]});Q212=makeQuery(id+"F1.imprint","IMPRINT",FACE,{"disambiguationData":[TD([[makeQuery(id+"F1.imprint","IMPRINT",EDGE,{"disambiguationData":[TD([[subQ2,1.0]])],"derivedFrom":subQ1}),1.0]])]});}
            var Q213;
            {var subQ0=sQuery(id+"F1.wireOp",EDGE,"E5.0.8.0");var subQ1=sQuery(id+"F1.wireOp",EDGE,"E3.7.0.0");var subQ2=makeQuery(id+"F1.imprint","INTERSECT",VERTEX,{"derivedFrom":[subQ1,subQ0]});Q213=makeQuery(id+"F1.imprint","IMPRINT",FACE,{"disambiguationData":[TD([[makeQuery(id+"F1.imprint","IMPRINT",EDGE,{"disambiguationData":[TD([[subQ2,1.0]])],"derivedFrom":subQ1}),1.0]])]});}
            var Q214;
            {var subQ0=sQuery(id+"F1.wireOp",EDGE,"E5.0.1.0");var subQ1=sQuery(id+"F1.wireOp",EDGE,"E3.3.0.0");var subQ2=makeQuery(id+"F1.imprint","INTERSECT",VERTEX,{"derivedFrom":[subQ1,subQ0]});Q214=makeQuery(id+"F1.imprint","IMPRINT",FACE,{"disambiguationData":[TD([[makeQuery(id+"F1.imprint","IMPRINT",EDGE,{"disambiguationData":[TD([[subQ2,-1.0]])],"derivedFrom":subQ1}),1.0]])]});}
            var Q215;
            {var subQ0=sQuery(id+"F1.wireOp",EDGE,"E5.0.4.0");var subQ1=sQuery(id+"F1.wireOp",EDGE,"E3.3.0.0");var subQ2=makeQuery(id+"F1.imprint","INTERSECT",VERTEX,{"derivedFrom":[subQ1,subQ0]});Q215=makeQuery(id+"F1.imprint","IMPRINT",FACE,{"disambiguationData":[TD([[makeQuery(id+"F1.imprint","IMPRINT",EDGE,{"disambiguationData":[TD([[subQ2,1.0]])],"derivedFrom":subQ1}),1.0]])]});}
            var Q216;
            {var subQ0=sQuery(id+"F1.wireOp",EDGE,"E5.0.4.1");var subQ1=sQuery(id+"F1.wireOp",EDGE,"E3.7.0.0");var subQ2=makeQuery(id+"F1.imprint","INTERSECT",VERTEX,{"derivedFrom":[subQ1,subQ0]});Q216=makeQuery(id+"F1.imprint","IMPRINT",FACE,{"disambiguationData":[TD([[makeQuery(id+"F1.imprint","IMPRINT",EDGE,{"disambiguationData":[TD([[subQ2,-1.0]])],"derivedFrom":subQ1}),1.0]])]});}
            var Q217;
            {var subQ0=sQuery(id+"F1.wireOp",EDGE,"E5.0.5.0");var subQ1=sQuery(id+"F1.wireOp",EDGE,"E3.7.0.0");var subQ2=makeQuery(id+"F1.imprint","INTERSECT",VERTEX,{"derivedFrom":[subQ1,subQ0]});Q217=makeQuery(id+"F1.imprint","IMPRINT",FACE,{"disambiguationData":[TD([[makeQuery(id+"F1.imprint","IMPRINT",EDGE,{"disambiguationData":[TD([[subQ2,-1.0]])],"derivedFrom":subQ1}),1.0]])]});}
            var Q218;
            {var subQ0=sQuery(id+"F1.wireOp",EDGE,"E5.0.1.0");var subQ1=sQuery(id+"F1.wireOp",EDGE,"E3.3.0.0");var subQ2=makeQuery(id+"F1.imprint","INTERSECT",VERTEX,{"derivedFrom":[subQ1,subQ0]});Q218=makeQuery(id+"F1.imprint","IMPRINT",FACE,{"disambiguationData":[TD([[makeQuery(id+"F1.imprint","IMPRINT",EDGE,{"disambiguationData":[TD([[subQ2,1.0]])],"derivedFrom":subQ1}),1.0]])]});}
            var Q219;
            {var subQ0=sQuery(id+"F1.wireOp",EDGE,"E5.0.4.0");var subQ1=sQuery(id+"F1.wireOp",EDGE,"E3.7.0.0");var subQ2=makeQuery(id+"F1.imprint","INTERSECT",VERTEX,{"derivedFrom":[subQ1,subQ0]});Q219=makeQuery(id+"F1.imprint","IMPRINT",FACE,{"disambiguationData":[TD([[makeQuery(id+"F1.imprint","IMPRINT",EDGE,{"disambiguationData":[TD([[subQ2,-1.0]])],"derivedFrom":subQ1}),1.0]])]});}
            var Q220;
            {var subQ0=sQuery(id+"F1.wireOp",EDGE,"E5.0.7.0");var subQ1=sQuery(id+"F1.wireOp",EDGE,"E3.7.0.0");var subQ2=makeQuery(id+"F1.imprint","INTERSECT",VERTEX,{"derivedFrom":[subQ1,subQ0]});Q220=makeQuery(id+"F1.imprint","IMPRINT",FACE,{"disambiguationData":[TD([[makeQuery(id+"F1.imprint","IMPRINT",EDGE,{"disambiguationData":[TD([[subQ2,1.0]])],"derivedFrom":subQ1}),1.0]])]});}
            var Q221;
            {var subQ0=sQuery(id+"F1.wireOp",EDGE,"E5.0.3.0");var subQ1=sQuery(id+"F1.wireOp",EDGE,"E3.3.0.0");var subQ2=makeQuery(id+"F1.imprint","INTERSECT",VERTEX,{"derivedFrom":[subQ1,subQ0]});Q221=makeQuery(id+"F1.imprint","IMPRINT",FACE,{"disambiguationData":[TD([[makeQuery(id+"F1.imprint","IMPRINT",EDGE,{"disambiguationData":[TD([[subQ2,-1.0]])],"derivedFrom":subQ1}),1.0]])]});}
            var Q222;
            {var subQ0=sQuery(id+"F1.wireOp",EDGE,"E5.0.5.1");var subQ1=sQuery(id+"F1.wireOp",EDGE,"E3.7.0.0");var subQ2=makeQuery(id+"F1.imprint","INTERSECT",VERTEX,{"derivedFrom":[subQ1,subQ0]});Q222=makeQuery(id+"F1.imprint","IMPRINT",FACE,{"disambiguationData":[TD([[makeQuery(id+"F1.imprint","IMPRINT",EDGE,{"disambiguationData":[TD([[subQ2,-1.0]])],"derivedFrom":subQ1}),1.0]])]});}
            var Q223;
            {var subQ0=sQuery(id+"F1.wireOp",EDGE,"E5.0.2.1");var subQ1=sQuery(id+"F1.wireOp",EDGE,"E3.3.0.0");var subQ2=makeQuery(id+"F1.imprint","INTERSECT",VERTEX,{"derivedFrom":[subQ1,subQ0]});Q223=makeQuery(id+"F1.imprint","IMPRINT",FACE,{"disambiguationData":[TD([[makeQuery(id+"F1.imprint","IMPRINT",EDGE,{"disambiguationData":[TD([[subQ2,1.0]])],"derivedFrom":subQ1}),1.0]])]});}
            var Q224;
            {var subQ0=sQuery(id+"F1.wireOp",EDGE,"E5.0.4.0");var subQ1=sQuery(id+"F1.wireOp",EDGE,"E3.4.0.0");var subQ2=makeQuery(id+"F1.imprint","INTERSECT",VERTEX,{"derivedFrom":[subQ1,subQ0]});Q224=makeQuery(id+"F1.imprint","IMPRINT",FACE,{"disambiguationData":[TD([[makeQuery(id+"F1.imprint","IMPRINT",EDGE,{"disambiguationData":[TD([[subQ2,-1.0]])],"derivedFrom":subQ1}),1.0]])]});}
            var Q225;
            {var subQ0=sQuery(id+"F1.wireOp",EDGE,"E3.2.0.1");var subQ1=sQuery(id+"F1.wireOp",EDGE,"E0.top");var subQ2=makeQuery(id+"F1.imprint","INTERSECT",VERTEX,{"derivedFrom":[subQ1,subQ0]});Q225=makeQuery(id+"F1.imprint","IMPRINT",FACE,{"disambiguationData":[TD([[makeQuery(id+"F1.imprint","IMPRINT",EDGE,{"disambiguationData":[TD([[subQ2,-1.0]])],"derivedFrom":subQ1}),-1.0]])]});}
            var Q226;
            {var subQ0=sQuery(id+"F1.wireOp",EDGE,"E3.7.0.1");var subQ1=sQuery(id+"F1.wireOp",EDGE,"E0.top");var subQ2=makeQuery(id+"F1.imprint","INTERSECT",VERTEX,{"derivedFrom":[subQ1,subQ0]});Q226=makeQuery(id+"F1.imprint","IMPRINT",FACE,{"disambiguationData":[TD([[makeQuery(id+"F1.imprint","IMPRINT",EDGE,{"disambiguationData":[TD([[subQ2,-1.0]])],"derivedFrom":subQ1}),-1.0]])]});}
            var Q227;
            {var subQ0=sQuery(id+"F1.wireOp",EDGE,"E3.5.0.0");var subQ1=sQuery(id+"F1.wireOp",EDGE,"E0.top");var subQ2=makeQuery(id+"F1.imprint","INTERSECT",VERTEX,{"derivedFrom":[subQ1,subQ0]});Q227=makeQuery(id+"F1.imprint","IMPRINT",FACE,{"disambiguationData":[TD([[makeQuery(id+"F1.imprint","IMPRINT",EDGE,{"disambiguationData":[TD([[subQ2,1.0]])],"derivedFrom":subQ1}),-1.0]])]});}
            var Q228;
            {var subQ0=sQuery(id+"F1.wireOp",EDGE,"E2.left");var subQ1=sQuery(id+"F1.wireOp",EDGE,"E0.top");var subQ2=makeQuery(id+"F1.imprint","INTERSECT",VERTEX,{"derivedFrom":[subQ1,subQ0]});Q228=makeQuery(id+"F1.imprint","IMPRINT",FACE,{"disambiguationData":[TD([[makeQuery(id+"F1.imprint","IMPRINT",EDGE,{"disambiguationData":[TD([[subQ2,1.0]])],"derivedFrom":subQ1}),-1.0]])]});}
            var Q229;
            {var subQ0=sQuery(id+"F1.wireOp",EDGE,"E3.3.0.0");var subQ1=sQuery(id+"F1.wireOp",EDGE,"E0.top");var subQ2=makeQuery(id+"F1.imprint","INTERSECT",VERTEX,{"derivedFrom":[subQ1,subQ0]});Q229=makeQuery(id+"F1.imprint","IMPRINT",FACE,{"disambiguationData":[TD([[makeQuery(id+"F1.imprint","IMPRINT",EDGE,{"disambiguationData":[TD([[subQ2,1.0]])],"derivedFrom":subQ1}),-1.0]])]});}
            var Q230;
            {var subQ0=sQuery(id+"F1.wireOp",EDGE,"E3.8.0.0");var subQ1=sQuery(id+"F1.wireOp",EDGE,"E0.top");var subQ2=makeQuery(id+"F1.imprint","INTERSECT",VERTEX,{"derivedFrom":[subQ1,subQ0]});Q230=makeQuery(id+"F1.imprint","IMPRINT",FACE,{"disambiguationData":[TD([[makeQuery(id+"F1.imprint","IMPRINT",EDGE,{"disambiguationData":[TD([[subQ2,1.0]])],"derivedFrom":subQ1}),-1.0]])]});}
            var Q231;
            {var subQ0=sQuery(id+"F1.wireOp",EDGE,"E3.1.0.1");var subQ1=sQuery(id+"F1.wireOp",EDGE,"E0.top");var subQ2=makeQuery(id+"F1.imprint","INTERSECT",VERTEX,{"derivedFrom":[subQ1,subQ0]});Q231=makeQuery(id+"F1.imprint","IMPRINT",FACE,{"disambiguationData":[TD([[makeQuery(id+"F1.imprint","IMPRINT",EDGE,{"disambiguationData":[TD([[subQ2,-1.0]])],"derivedFrom":subQ1}),-1.0]])]});}
            var Q232;
            {var subQ0=sQuery(id+"F1.wireOp",EDGE,"E3.6.0.0");var subQ1=sQuery(id+"F1.wireOp",EDGE,"E0.top");var subQ2=makeQuery(id+"F1.imprint","INTERSECT",VERTEX,{"derivedFrom":[subQ1,subQ0]});Q232=makeQuery(id+"F1.imprint","IMPRINT",FACE,{"disambiguationData":[TD([[makeQuery(id+"F1.imprint","IMPRINT",EDGE,{"disambiguationData":[TD([[subQ2,1.0]])],"derivedFrom":subQ1}),-1.0]])]});}
            var Q233;
            {var subQ0=sQuery(id+"F1.wireOp",EDGE,"E3.4.0.1");var subQ1=sQuery(id+"F1.wireOp",EDGE,"E0.top");var subQ2=makeQuery(id+"F1.imprint","INTERSECT",VERTEX,{"derivedFrom":[subQ1,subQ0]});Q233=makeQuery(id+"F1.imprint","IMPRINT",FACE,{"disambiguationData":[TD([[makeQuery(id+"F1.imprint","IMPRINT",EDGE,{"disambiguationData":[TD([[subQ2,-1.0]])],"derivedFrom":subQ1}),-1.0]])]});}
            var Q234;
            {var subQ0=sQuery(id+"F1.wireOp",EDGE,"E5.0.8.1");var subQ1=sQuery(id+"F1.wireOp",EDGE,"E0.left");var subQ2=makeQuery(id+"F1.imprint","INTERSECT",VERTEX,{"derivedFrom":[subQ1,subQ0]});Q234=makeQuery(id+"F1.imprint","IMPRINT",FACE,{"disambiguationData":[TD([[makeQuery(id+"F1.imprint","IMPRINT",EDGE,{"disambiguationData":[TD([[subQ2,1.0]])],"derivedFrom":subQ1}),-1.0]])]});}
            var Q235;
            {var subQ0=sQuery(id+"F1.wireOp",EDGE,"E5.0.7.0");var subQ1=sQuery(id+"F1.wireOp",EDGE,"E0.left");var subQ2=makeQuery(id+"F1.imprint","INTERSECT",VERTEX,{"derivedFrom":[subQ1,subQ0]});Q235=makeQuery(id+"F1.imprint","IMPRINT",FACE,{"disambiguationData":[TD([[makeQuery(id+"F1.imprint","IMPRINT",EDGE,{"disambiguationData":[TD([[subQ2,-1.0]])],"derivedFrom":subQ1}),-1.0]])]});}
            var Q236;
            {var subQ0=sQuery(id+"F1.wireOp",EDGE,"E5.0.6.1");var subQ1=sQuery(id+"F1.wireOp",EDGE,"E0.left");var subQ2=makeQuery(id+"F1.imprint","INTERSECT",VERTEX,{"derivedFrom":[subQ1,subQ0]});Q236=makeQuery(id+"F1.imprint","IMPRINT",FACE,{"disambiguationData":[TD([[makeQuery(id+"F1.imprint","IMPRINT",EDGE,{"disambiguationData":[TD([[subQ2,1.0]])],"derivedFrom":subQ1}),-1.0]])]});}
            var Q237;
            {var subQ0=sQuery(id+"F1.wireOp",EDGE,"E5.0.5.0");var subQ1=sQuery(id+"F1.wireOp",EDGE,"E0.left");var subQ2=makeQuery(id+"F1.imprint","INTERSECT",VERTEX,{"derivedFrom":[subQ1,subQ0]});Q237=makeQuery(id+"F1.imprint","IMPRINT",FACE,{"disambiguationData":[TD([[makeQuery(id+"F1.imprint","IMPRINT",EDGE,{"disambiguationData":[TD([[subQ2,-1.0]])],"derivedFrom":subQ1}),-1.0]])]});}
            var Q238;
            {var subQ0=sQuery(id+"F1.wireOp",EDGE,"E5.0.4.0");var subQ1=sQuery(id+"F1.wireOp",EDGE,"E0.left");var subQ2=makeQuery(id+"F1.imprint","INTERSECT",VERTEX,{"derivedFrom":[subQ1,subQ0]});Q238=makeQuery(id+"F1.imprint","IMPRINT",FACE,{"disambiguationData":[TD([[makeQuery(id+"F1.imprint","IMPRINT",EDGE,{"disambiguationData":[TD([[subQ2,-1.0]])],"derivedFrom":subQ1}),-1.0]])]});}
            var Q239;
            {var subQ0=sQuery(id+"F1.wireOp",EDGE,"E5.0.3.1");var subQ1=sQuery(id+"F1.wireOp",EDGE,"E0.left");var subQ2=makeQuery(id+"F1.imprint","INTERSECT",VERTEX,{"derivedFrom":[subQ1,subQ0]});Q239=makeQuery(id+"F1.imprint","IMPRINT",FACE,{"disambiguationData":[TD([[makeQuery(id+"F1.imprint","IMPRINT",EDGE,{"disambiguationData":[TD([[subQ2,1.0]])],"derivedFrom":subQ1}),-1.0]])]});}
            var Q240;
            {var subQ0=sQuery(id+"F1.wireOp",EDGE,"E5.0.2.1");var subQ1=sQuery(id+"F1.wireOp",EDGE,"E0.left");var subQ2=makeQuery(id+"F1.imprint","INTERSECT",VERTEX,{"derivedFrom":[subQ1,subQ0]});Q240=makeQuery(id+"F1.imprint","IMPRINT",FACE,{"disambiguationData":[TD([[makeQuery(id+"F1.imprint","IMPRINT",EDGE,{"disambiguationData":[TD([[subQ2,1.0]])],"derivedFrom":subQ1}),-1.0]])]});}
            var Q241;
            {var subQ0=sQuery(id+"F1.wireOp",EDGE,"E5.0.8.1");var subQ1=sQuery(id+"F1.wireOp",EDGE,"E0.right");var subQ2=makeQuery(id+"F1.imprint","INTERSECT",VERTEX,{"derivedFrom":[subQ1,subQ0]});Q241=makeQuery(id+"F1.imprint","IMPRINT",FACE,{"disambiguationData":[TD([[makeQuery(id+"F1.imprint","IMPRINT",EDGE,{"disambiguationData":[TD([[subQ2,1.0]])],"derivedFrom":subQ1}),1.0]])]});}
            var Q242;
            {var subQ0=sQuery(id+"F1.wireOp",EDGE,"E5.0.7.0");var subQ1=sQuery(id+"F1.wireOp",EDGE,"E0.right");var subQ2=makeQuery(id+"F1.imprint","INTERSECT",VERTEX,{"derivedFrom":[subQ1,subQ0]});Q242=makeQuery(id+"F1.imprint","IMPRINT",FACE,{"disambiguationData":[TD([[makeQuery(id+"F1.imprint","IMPRINT",EDGE,{"disambiguationData":[TD([[subQ2,-1.0]])],"derivedFrom":subQ1}),1.0]])]});}
            var Q243;
            {var subQ0=sQuery(id+"F1.wireOp",EDGE,"E5.0.5.1");var subQ1=sQuery(id+"F1.wireOp",EDGE,"E0.right");var subQ2=makeQuery(id+"F1.imprint","INTERSECT",VERTEX,{"derivedFrom":[subQ1,subQ0]});Q243=makeQuery(id+"F1.imprint","IMPRINT",FACE,{"disambiguationData":[TD([[makeQuery(id+"F1.imprint","IMPRINT",EDGE,{"disambiguationData":[TD([[subQ2,1.0]])],"derivedFrom":subQ1}),1.0]])]});}
            var Q244;
            {var subQ0=sQuery(id+"F1.wireOp",EDGE,"E5.0.4.1");var subQ1=sQuery(id+"F1.wireOp",EDGE,"E0.right");var subQ2=makeQuery(id+"F1.imprint","INTERSECT",VERTEX,{"derivedFrom":[subQ1,subQ0]});Q244=makeQuery(id+"F1.imprint","IMPRINT",FACE,{"disambiguationData":[TD([[makeQuery(id+"F1.imprint","IMPRINT",EDGE,{"disambiguationData":[TD([[subQ2,1.0]])],"derivedFrom":subQ1}),1.0]])]});}
            var Q245;
            {var subQ0=sQuery(id+"F1.wireOp",EDGE,"E5.0.3.1");var subQ1=sQuery(id+"F1.wireOp",EDGE,"E0.right");var subQ2=makeQuery(id+"F1.imprint","INTERSECT",VERTEX,{"derivedFrom":[subQ1,subQ0]});Q245=makeQuery(id+"F1.imprint","IMPRINT",FACE,{"disambiguationData":[TD([[makeQuery(id+"F1.imprint","IMPRINT",EDGE,{"disambiguationData":[TD([[subQ2,1.0]])],"derivedFrom":subQ1}),1.0]])]});}
            var Q246;
            {var subQ0=sQuery(id+"F1.wireOp",EDGE,"E5.0.2.1");var subQ1=sQuery(id+"F1.wireOp",EDGE,"E0.right");var subQ2=makeQuery(id+"F1.imprint","INTERSECT",VERTEX,{"derivedFrom":[subQ1,subQ0]});Q246=makeQuery(id+"F1.imprint","IMPRINT",FACE,{"disambiguationData":[TD([[makeQuery(id+"F1.imprint","IMPRINT",EDGE,{"disambiguationData":[TD([[subQ2,1.0]])],"derivedFrom":subQ1}),1.0]])]});}
            var Q247;
            {var subQ0=sQuery(id+"F1.wireOp",EDGE,"E5.0.1.0");var subQ1=sQuery(id+"F1.wireOp",EDGE,"E0.left");var subQ2=makeQuery(id+"F1.imprint","INTERSECT",VERTEX,{"derivedFrom":[subQ1,subQ0]});Q247=makeQuery(id+"F1.imprint","IMPRINT",FACE,{"disambiguationData":[TD([[makeQuery(id+"F1.imprint","IMPRINT",EDGE,{"disambiguationData":[TD([[subQ2,-1.0]])],"derivedFrom":subQ1}),-1.0]])]});}
            var Q248;
            {var subQ0=sQuery(id+"F1.wireOp",EDGE,"E4.bottom");var subQ1=sQuery(id+"F1.wireOp",EDGE,"E0.left");var subQ2=makeQuery(id+"F1.imprint","INTERSECT",VERTEX,{"derivedFrom":[subQ1,subQ0]});Q248=makeQuery(id+"F1.imprint","IMPRINT",FACE,{"disambiguationData":[TD([[makeQuery(id+"F1.imprint","IMPRINT",EDGE,{"disambiguationData":[TD([[subQ2,-1.0]])],"derivedFrom":subQ1}),-1.0]])]});}
            var Q249;
            {var subQ0=sQuery(id+"F1.wireOp",EDGE,"E3.8.0.1");var subQ1=sQuery(id+"F1.wireOp",EDGE,"E0.bottom");var subQ2=makeQuery(id+"F1.imprint","INTERSECT",VERTEX,{"derivedFrom":[subQ1,subQ0]});Q249=makeQuery(id+"F1.imprint","IMPRINT",FACE,{"disambiguationData":[TD([[makeQuery(id+"F1.imprint","IMPRINT",EDGE,{"disambiguationData":[TD([[subQ2,-1.0]])],"derivedFrom":subQ1}),1.0]])]});}
            var Q250;
            {var subQ0=sQuery(id+"F1.wireOp",EDGE,"E3.7.0.1");var subQ1=sQuery(id+"F1.wireOp",EDGE,"E0.bottom");var subQ2=makeQuery(id+"F1.imprint","INTERSECT",VERTEX,{"derivedFrom":[subQ1,subQ0]});Q250=makeQuery(id+"F1.imprint","IMPRINT",FACE,{"disambiguationData":[TD([[makeQuery(id+"F1.imprint","IMPRINT",EDGE,{"disambiguationData":[TD([[subQ2,-1.0]])],"derivedFrom":subQ1}),1.0]])]});}
            var Q251;
            {var subQ0=sQuery(id+"F1.wireOp",EDGE,"E3.6.0.0");var subQ1=sQuery(id+"F1.wireOp",EDGE,"E0.bottom");var subQ2=makeQuery(id+"F1.imprint","INTERSECT",VERTEX,{"derivedFrom":[subQ1,subQ0]});Q251=makeQuery(id+"F1.imprint","IMPRINT",FACE,{"disambiguationData":[TD([[makeQuery(id+"F1.imprint","IMPRINT",EDGE,{"disambiguationData":[TD([[subQ2,1.0]])],"derivedFrom":subQ1}),1.0]])]});}
            var Q252;
            {var subQ0=sQuery(id+"F1.wireOp",EDGE,"E3.5.0.0");var subQ1=sQuery(id+"F1.wireOp",EDGE,"E0.bottom");var subQ2=makeQuery(id+"F1.imprint","INTERSECT",VERTEX,{"derivedFrom":[subQ1,subQ0]});Q252=makeQuery(id+"F1.imprint","IMPRINT",FACE,{"disambiguationData":[TD([[makeQuery(id+"F1.imprint","IMPRINT",EDGE,{"disambiguationData":[TD([[subQ2,1.0]])],"derivedFrom":subQ1}),1.0]])]});}
            var Q253;
            {var subQ0=sQuery(id+"F1.wireOp",EDGE,"E3.4.0.0");var subQ1=sQuery(id+"F1.wireOp",EDGE,"E0.bottom");var subQ2=makeQuery(id+"F1.imprint","INTERSECT",VERTEX,{"derivedFrom":[subQ1,subQ0]});Q253=makeQuery(id+"F1.imprint","IMPRINT",FACE,{"disambiguationData":[TD([[makeQuery(id+"F1.imprint","IMPRINT",EDGE,{"disambiguationData":[TD([[subQ2,1.0]])],"derivedFrom":subQ1}),1.0]])]});}
            var Q254;
            {var subQ0=sQuery(id+"F1.wireOp",EDGE,"E3.3.0.0");var subQ1=sQuery(id+"F1.wireOp",EDGE,"E0.bottom");var subQ2=makeQuery(id+"F1.imprint","INTERSECT",VERTEX,{"derivedFrom":[subQ1,subQ0]});Q254=makeQuery(id+"F1.imprint","IMPRINT",FACE,{"disambiguationData":[TD([[makeQuery(id+"F1.imprint","IMPRINT",EDGE,{"disambiguationData":[TD([[subQ2,1.0]])],"derivedFrom":subQ1}),1.0]])]});}
            var Q255;
            {var subQ0=sQuery(id+"F1.wireOp",EDGE,"E3.2.0.0");var subQ1=sQuery(id+"F1.wireOp",EDGE,"E0.bottom");var subQ2=makeQuery(id+"F1.imprint","INTERSECT",VERTEX,{"derivedFrom":[subQ1,subQ0]});Q255=makeQuery(id+"F1.imprint","IMPRINT",FACE,{"disambiguationData":[TD([[makeQuery(id+"F1.imprint","IMPRINT",EDGE,{"disambiguationData":[TD([[subQ2,1.0]])],"derivedFrom":subQ1}),1.0]])]});}
            var Q256;
            {var subQ0=sQuery(id+"F1.wireOp",EDGE,"E3.1.0.0");var subQ1=sQuery(id+"F1.wireOp",EDGE,"E0.bottom");var subQ2=makeQuery(id+"F1.imprint","INTERSECT",VERTEX,{"derivedFrom":[subQ1,subQ0]});Q256=makeQuery(id+"F1.imprint","IMPRINT",FACE,{"disambiguationData":[TD([[makeQuery(id+"F1.imprint","IMPRINT",EDGE,{"disambiguationData":[TD([[subQ2,1.0]])],"derivedFrom":subQ1}),1.0]])]});}
            var Q257;
            {var subQ0=sQuery(id+"F1.wireOp",EDGE,"E2.left");var subQ1=sQuery(id+"F1.wireOp",EDGE,"E0.bottom");var subQ2=makeQuery(id+"F1.imprint","INTERSECT",VERTEX,{"derivedFrom":[subQ1,subQ0]});Q257=makeQuery(id+"F1.imprint","IMPRINT",FACE,{"disambiguationData":[TD([[makeQuery(id+"F1.imprint","IMPRINT",EDGE,{"disambiguationData":[TD([[subQ2,1.0]])],"derivedFrom":subQ1}),1.0]])]});}
            var Q258;
            {var subQ0=sQuery(id+"F1.wireOp",EDGE,"E4.bottom");var subQ1=sQuery(id+"F1.wireOp",EDGE,"E0.right");var subQ2=makeQuery(id+"F1.imprint","INTERSECT",VERTEX,{"derivedFrom":[subQ1,subQ0]});Q258=makeQuery(id+"F1.imprint","IMPRINT",FACE,{"disambiguationData":[TD([[makeQuery(id+"F1.imprint","IMPRINT",EDGE,{"disambiguationData":[TD([[subQ2,-1.0]])],"derivedFrom":subQ1}),1.0]])]});}
            var Q259;
            {var subQ0=sQuery(id+"F1.wireOp",EDGE,"E5.0.1.0");var subQ1=sQuery(id+"F1.wireOp",EDGE,"E0.right");var subQ2=makeQuery(id+"F1.imprint","INTERSECT",VERTEX,{"derivedFrom":[subQ1,subQ0]});Q259=makeQuery(id+"F1.imprint","IMPRINT",FACE,{"disambiguationData":[TD([[makeQuery(id+"F1.imprint","IMPRINT",EDGE,{"disambiguationData":[TD([[subQ2,-1.0]])],"derivedFrom":subQ1}),1.0]])]});}
            var Q260;
            {var subQ0=sQuery(id+"F1.wireOp",EDGE,"E5.0.6.1");var subQ1=sQuery(id+"F1.wireOp",EDGE,"E0.right");var subQ2=makeQuery(id+"F1.imprint","INTERSECT",VERTEX,{"derivedFrom":[subQ1,subQ0]});Q260=makeQuery(id+"F1.imprint","IMPRINT",FACE,{"disambiguationData":[TD([[makeQuery(id+"F1.imprint","IMPRINT",EDGE,{"disambiguationData":[TD([[subQ2,1.0]])],"derivedFrom":subQ1}),1.0]])]});}
            extrude(context, id + "F3", {"entities" : qUnion([Q0, Q1, Q2, Q3, Q4, Q5, Q6, Q7, Q8, Q9, Q10, Q11, Q12, Q13, Q14, Q15, Q16, Q17, Q18, Q19, Q20, Q21, Q22, Q23, Q24, Q25, Q26, Q27, Q28, Q29, Q30, Q31, Q32, Q33, Q34, Q35, Q36, Q37, Q38, Q39, Q40, Q41, Q42, Q43, Q44, Q45, Q46, Q47, Q48, Q49, Q50, Q51, Q52, Q53, Q54, Q55, Q56, Q57, Q58, Q59, Q60, Q61, Q62, Q63, Q64, Q65, Q66, Q67, Q68, Q69, Q70, Q71, Q72, Q73, Q74, Q75, Q76, Q77, Q78, Q79, Q80, Q81, Q82, Q83, Q84, Q85, Q86, Q87, Q88, Q89, Q90, Q91, Q92, Q93, Q94, Q95, Q96, Q97, Q98, Q99, Q100, Q101, Q102, Q103, Q104, Q105, Q106, Q107, Q108, Q109, Q110, Q111, Q112, Q113, Q114, Q115, Q116, Q117, Q118, Q119, Q120, Q121, Q122, Q123, Q124, Q125, Q126, Q127, Q128, Q129, Q130, Q131, Q132, Q133, Q134, Q135, Q136, Q137, Q138, Q139, Q140, Q141, Q142, Q143, Q144, Q145, Q146, Q147, Q148, Q149, Q150, Q151, Q152, Q153, Q154, Q155, Q156, Q157, Q158, Q159, Q160, Q161, Q162, Q163, Q164, Q165, Q166, Q167, Q168, Q169, Q170, Q171, Q172, Q173, Q174, Q175, Q176, Q177, Q178, Q179, Q180, Q181, Q182, Q183, Q184, Q185, Q186, Q187, Q188, Q189, Q190, Q191, Q192, Q193, Q194, Q195, Q196, Q197, Q198, Q199, Q200, Q201, Q202, Q203, Q204, Q205, Q206, Q207, Q208, Q209, Q210, Q211, Q212, Q213, Q214, Q215, Q216, Q217, Q218, Q219, Q220, Q221, Q222, Q223, Q224, Q225, Q226, Q227, Q228, Q229, Q230, Q231, Q232, Q233, Q234, Q235, Q236, Q237, Q238, Q239, Q240, Q241, Q242, Q243, Q244, Q245, Q246, Q247, Q248, Q249, Q250, Q251, Q252, Q253, Q254, Q255, Q256, Q257, Q258, Q259, Q260]), "operationType" : NewBodyOperationType.ADD, "depth" : 10 * mm, "offsetDistance" : 25 * mm});
        }
        {
            var Q0;
            Q0=makeQuery(id+"F2.opExtrude","SWEPT_EDGE",EDGE,{"disambiguationData":[OSD([sQuery(id+"F1.wireOp",EDGE,"E1.top"),sQuery(id+"F1.wireOp",EDGE,"E1.right")])]});
            var Q1;
            Q1=makeQuery(id+"F2.opExtrude","SWEPT_EDGE",EDGE,{"disambiguationData":[OSD([sQuery(id+"F1.wireOp",EDGE,"E1.top"),sQuery(id+"F1.wireOp",EDGE,"E1.left")])]});
            var Q2;
            Q2=makeQuery(id+"F2.opExtrude","SWEPT_EDGE",EDGE,{"disambiguationData":[OSD([sQuery(id+"F1.wireOp",EDGE,"E1.bottom"),sQuery(id+"F1.wireOp",EDGE,"E1.left")])]});
            var Q3;
            Q3=makeQuery(id+"F2.opExtrude","SWEPT_EDGE",EDGE,{"disambiguationData":[OSD([sQuery(id+"F1.wireOp",EDGE,"E1.bottom"),sQuery(id+"F1.wireOp",EDGE,"E1.right")])]});
            fillet(context, id + "F4", {"entities" : qUnion([Q0, Q1, Q2, Q3]), "radius" : (getVariable(context, 'p')) * mm, "tangentPropagation" : true, "allowEdgeOverflow" : false});
        }
        {
            var Q0;
            Q0=makeQuery(id+"F2.opExtrude","CAP_EDGE",EDGE,{"disambiguationData":[OSD([sQuery(id+"F1.wireOp",EDGE,"E1.bottom")])],"isStart":true});
            chamfer(context, id + "F5", {"entities" : qUnion([Q0]), "chamferType" : ChamferType.TWO_OFFSETS, "width1" : .75 * mm, "oppositeDirection" : false, "width2" : 15 * mm, "tangentPropagation" : true});
        }
    });
